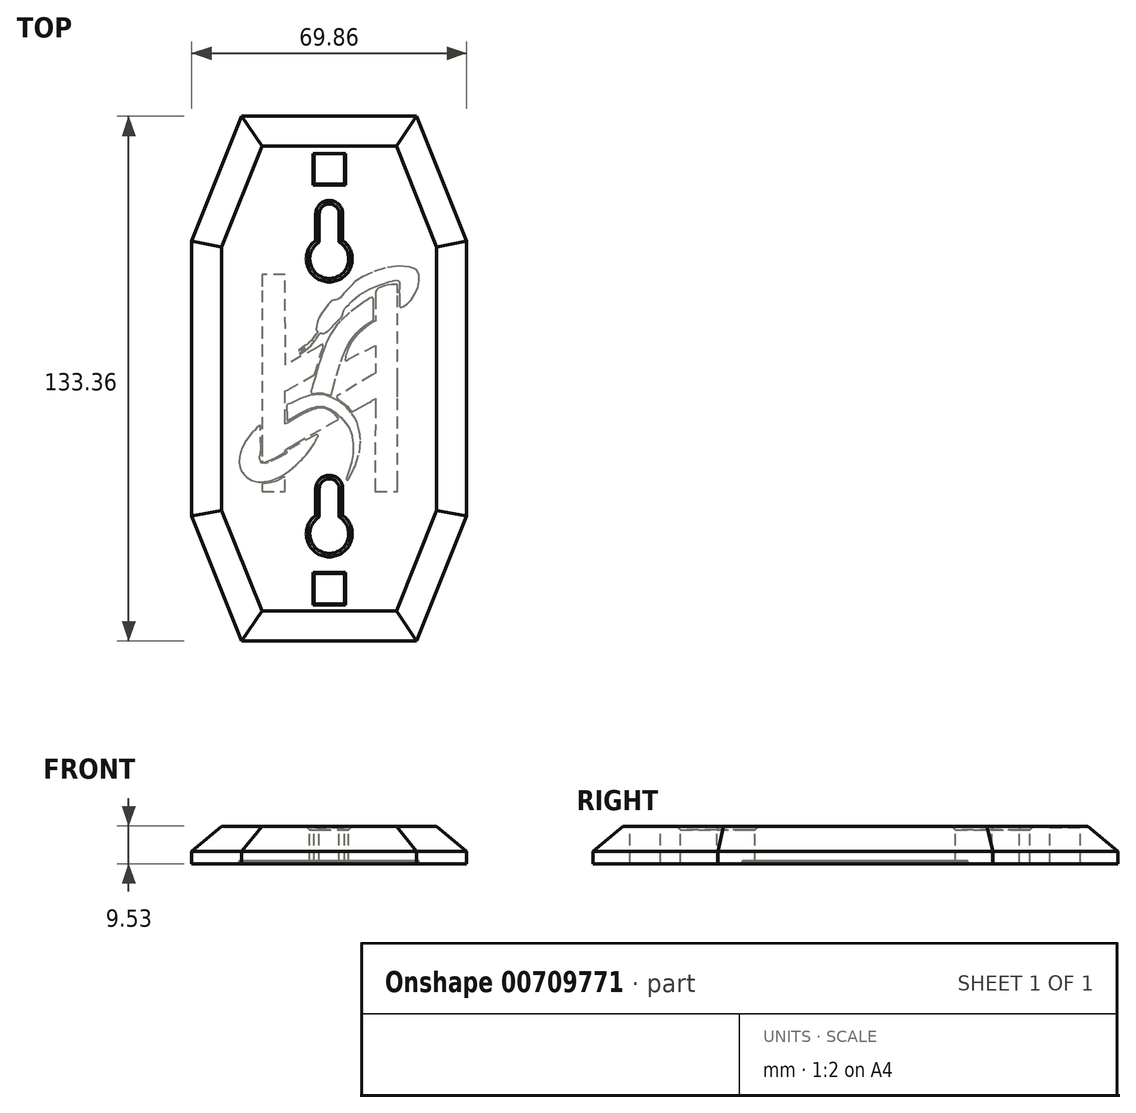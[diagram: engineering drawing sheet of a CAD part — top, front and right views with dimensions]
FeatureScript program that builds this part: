
annotation { "Feature Type Name" : "Feature", "Feature Type Description" : "" }
export const myFeature = defineFeature(function(context is Context, id is Id, definition is map)
    precondition{}
    {
        {
            var Q0;
            Q0=qCreatedBy(makeId("Top.planeOp"),FACE);
            var sketch = newSketch(context, id + "F0", { "sketchPlane" : qUnion([Q0])});
            skLineSegment(sketch, "E0.bottom", {"start": v(22.23, 66.68) * mm, "end": v(-22.22, 66.68) * mm});
            skLineSegment(sketch, "E0.top", {"start": v(22.22, -66.68) * mm, "end": v(-22.23, -66.68) * mm});
            skLineSegment(sketch, "E1.left", {"start": v(34.92, -34.93) * mm, "end": v(34.93, 34.92) * mm});
            skLineSegment(sketch, "E1.right", {"start": v(-34.93, -34.92) * mm, "end": v(-34.92, 34.93) * mm});
            skLineSegment(sketch, "E2", {"start": v(22.23, 66.67) * mm, "end": v(34.93, 34.92) * mm});
            skLineSegment(sketch, "E3", {"start": v(-22.22, 66.67) * mm, "end": v(-34.92, 34.93) * mm});
            skLineSegment(sketch, "E4", {"start": v(-34.93, -34.92) * mm, "end": v(-22.23, -66.68) * mm});
            skLineSegment(sketch, "E5", {"start": v(22.22, -66.68) * mm, "end": v(34.92, -34.93) * mm});
            skLineSegment(sketch, "E6", {"start": v(-17.37, -2.42) * mm, "end": v(-17.37, -0.22) * mm});
            skLineSegment(sketch, "E7", {"start": v(-17.37, -0.22) * mm, "end": v(-17.35, 21.74) * mm});
            skLineSegment(sketch, "E8", {"start": v(-17.35, 21.74) * mm, "end": v(-17.33, 23.94) * mm});
            skLineSegment(sketch, "E9", {"start": v(-17.33, 23.94) * mm, "end": v(-16.97, 23.94) * mm});
            skLineSegment(sketch, "E10", {"start": v(-16.97, 23.94) * mm, "end": v(-15.85, 23.92) * mm});
            skLineSegment(sketch, "E11", {"start": v(-15.85, 23.92) * mm, "end": v(-14.84, 23.83) * mm});
            skLineSegment(sketch, "E12", {"start": v(-14.84, 23.83) * mm, "end": v(-13.88, 23.56) * mm});
            skLineSegment(sketch, "E13", {"start": v(-13.88, 23.56) * mm, "end": v(-12.87, 23.15) * mm});
            skLineSegment(sketch, "E14", {"start": v(-12.87, 23.15) * mm, "end": v(-12.53, 23) * mm});
            skLineSegment(sketch, "E15", {"start": v(-12.53, 23) * mm, "end": v(-12.38, 22.93) * mm});
            skLineSegment(sketch, "E16", {"start": v(-12.38, 22.93) * mm, "end": v(-12, 22.53) * mm});
            skLineSegment(sketch, "E17", {"start": v(-12, 22.53) * mm, "end": v(-11.76, 21.9) * mm});
            skLineSegment(sketch, "E18", {"start": v(-11.76, 21.9) * mm, "end": v(-11.7, 21.25) * mm});
            skLineSegment(sketch, "E19", {"start": v(-11.7, 21.25) * mm, "end": v(-11.7, 20.85) * mm});
            skLineSegment(sketch, "E20", {"start": v(-11.7, 20.85) * mm, "end": v(-11.7, 20.71) * mm});
            skLineSegment(sketch, "E21", {"start": v(-11.7, 20.71) * mm, "end": v(-11.7, 14.62) * mm});
            skLineSegment(sketch, "E22", {"start": v(-11.7, 14.62) * mm, "end": v(-11.39, 14.51) * mm});
            skLineSegment(sketch, "E23", {"start": v(-11.39, 14.51) * mm, "end": v(-10.5, 14.04) * mm});
            skLineSegment(sketch, "E24", {"start": v(-10.5, 14.04) * mm, "end": v(-9.42, 13.27) * mm});
            skLineSegment(sketch, "E25", {"start": v(-9.42, 13.27) * mm, "end": v(-8.4, 12.4) * mm});
            skLineSegment(sketch, "E26", {"start": v(-8.4, 12.4) * mm, "end": v(-7.66, 11.74) * mm});
            skLineSegment(sketch, "E27", {"start": v(-7.66, 11.74) * mm, "end": v(-7.4, 11.53) * mm});
            skLineSegment(sketch, "E28", {"start": v(-7.4, 11.53) * mm, "end": v(-7.15, 11.32) * mm});
            skLineSegment(sketch, "E29", {"start": v(-7.15, 11.32) * mm, "end": v(-6.5, 10.61) * mm});
            skLineSegment(sketch, "E30", {"start": v(-6.5, 10.61) * mm, "end": v(-5.78, 9.57) * mm});
            skLineSegment(sketch, "E31", {"start": v(-5.78, 9.57) * mm, "end": v(-5.18, 8.44) * mm});
            skLineSegment(sketch, "E32", {"start": v(-5.18, 8.44) * mm, "end": v(-4.78, 7.57) * mm});
            skLineSegment(sketch, "E33", {"start": v(-4.78, 7.57) * mm, "end": v(-4.66, 7.28) * mm});
            skLineSegment(sketch, "E34", {"start": v(-4.66, 7.28) * mm, "end": v(-4.63, 7.18) * mm});
            skLineSegment(sketch, "E35", {"start": v(-4.63, 7.18) * mm, "end": v(-4.53, 6.89) * mm});
            skLineSegment(sketch, "E36", {"start": v(-4.53, 6.89) * mm, "end": v(-4.36, 6.39) * mm});
            skLineSegment(sketch, "E37", {"start": v(-4.36, 6.39) * mm, "end": v(-4.2, 5.84) * mm});
            skLineSegment(sketch, "E38", {"start": v(-4.2, 5.84) * mm, "end": v(-4.07, 5.33) * mm});
            skLineSegment(sketch, "E39", {"start": v(-4.07, 5.33) * mm, "end": v(-4.04, 4.91) * mm});
            skLineSegment(sketch, "E40", {"start": v(-4.04, 4.91) * mm, "end": v(-4.14, 4.66) * mm});
            skLineSegment(sketch, "E41", {"start": v(-4.14, 4.66) * mm, "end": v(-4.43, 4.66) * mm});
            skLineSegment(sketch, "E42", {"start": v(-4.43, 4.66) * mm, "end": v(-4.82, 4.88) * mm});
            skLineSegment(sketch, "E43", {"start": v(-4.82, 4.88) * mm, "end": v(-4.94, 4.97) * mm});
            skLineSegment(sketch, "E44", {"start": v(-4.94, 4.97) * mm, "end": v(-11.7, 8.43) * mm});
            skLineSegment(sketch, "E45", {"start": v(-11.7, 8.43) * mm, "end": v(-11.7, 1.45) * mm});
            skLineSegment(sketch, "E46", {"start": v(-11.7, 1.45) * mm, "end": v(-10.9, 1) * mm});
            skLineSegment(sketch, "E47", {"start": v(-10.9, 1) * mm, "end": v(-6.78, -1.51) * mm});
            skLineSegment(sketch, "E48", {"start": v(-6.78, -1.51) * mm, "end": v(-2.66, -4.02) * mm});
            skLineSegment(sketch, "E49", {"start": v(-2.66, -4.02) * mm, "end": v(-1.85, -4.48) * mm});
            skLineSegment(sketch, "E50", {"start": v(-1.85, -4.48) * mm, "end": v(-1.81, -4.54) * mm});
            skLineSegment(sketch, "E51", {"start": v(-1.81, -4.54) * mm, "end": v(-1.93, -4.9) * mm});
            skLineSegment(sketch, "E52", {"start": v(-1.93, -4.9) * mm, "end": v(-2.54, -5.38) * mm});
            skLineSegment(sketch, "E53", {"start": v(-2.54, -5.38) * mm, "end": v(-3.43, -6) * mm});
            skLineSegment(sketch, "E54", {"start": v(-3.43, -6) * mm, "end": v(-4.13, -6.56) * mm});
            skLineSegment(sketch, "E55", {"start": v(-4.13, -6.56) * mm, "end": v(-4.33, -6.78) * mm});
            skLineSegment(sketch, "E56", {"start": v(-4.33, -6.78) * mm, "end": v(-4.52, -6.96) * mm});
            skLineSegment(sketch, "E57", {"start": v(-4.52, -6.96) * mm, "end": v(-5.06, -7.56) * mm});
            skLineSegment(sketch, "E58", {"start": v(-5.06, -7.56) * mm, "end": v(-5.52, -8.12) * mm});
            skLineSegment(sketch, "E59", {"start": v(-5.52, -8.12) * mm, "end": v(-5.87, -8.36) * mm});
            skLineSegment(sketch, "E60", {"start": v(-5.87, -8.36) * mm, "end": v(-6.17, -8.24) * mm});
            skLineSegment(sketch, "E61", {"start": v(-6.17, -8.24) * mm, "end": v(-6.23, -8.17) * mm});
            skLineSegment(sketch, "E62", {"start": v(-6.23, -8.17) * mm, "end": v(-6.63, -7.95) * mm});
            skLineSegment(sketch, "E63", {"start": v(-6.63, -7.95) * mm, "end": v(-7.83, -7.3) * mm});
            skLineSegment(sketch, "E64", {"start": v(-7.83, -7.3) * mm, "end": v(-8.99, -6.65) * mm});
            skLineSegment(sketch, "E65", {"start": v(-8.99, -6.65) * mm, "end": v(-9.8, -6.19) * mm});
            skLineSegment(sketch, "E66", {"start": v(-9.8, -6.19) * mm, "end": v(-10.36, -5.87) * mm});
            skLineSegment(sketch, "E67", {"start": v(-10.36, -5.87) * mm, "end": v(-10.74, -5.64) * mm});
            skLineSegment(sketch, "E68", {"start": v(-10.74, -5.64) * mm, "end": v(-11.03, -5.46) * mm});
            skLineSegment(sketch, "E69", {"start": v(-11.03, -5.46) * mm, "end": v(-11.32, -5.28) * mm});
            skLineSegment(sketch, "E70", {"start": v(-11.32, -5.28) * mm, "end": v(-11.6, -5.11) * mm});
            skLineSegment(sketch, "E71", {"start": v(-11.6, -5.11) * mm, "end": v(-11.7, -5.06) * mm});
            skLineSegment(sketch, "E72", {"start": v(-11.7, -5.06) * mm, "end": v(-11.7, -7.02) * mm});
            skLineSegment(sketch, "E73", {"start": v(-11.7, -7.02) * mm, "end": v(-11.68, -26.64) * mm});
            skLineSegment(sketch, "E74", {"start": v(-11.68, -26.64) * mm, "end": v(-11.68, -28.6) * mm});
            skLineSegment(sketch, "E75", {"start": v(-11.68, -28.6) * mm, "end": v(-17.38, -28.6) * mm});
            skLineSegment(sketch, "E76", {"start": v(-17.38, -28.6) * mm, "end": v(-17.38, -26.42) * mm});
            skLineSegment(sketch, "E77", {"start": v(-17.38, -26.42) * mm, "end": v(-17.37, -4.6) * mm});
            skLineSegment(sketch, "E78", {"start": v(-17.37, -4.6) * mm, "end": v(-17.37, -2.42) * mm});
            skLineSegment(sketch, "E79", {"start": v(11.23, -25.1) * mm, "end": v(11.28, -25.05) * mm});
            skLineSegment(sketch, "E80", {"start": v(11.28, -25.05) * mm, "end": v(11.49, -25) * mm});
            skLineSegment(sketch, "E81", {"start": v(11.49, -25) * mm, "end": v(11.7, -25.09) * mm});
            skLineSegment(sketch, "E82", {"start": v(11.7, -25.09) * mm, "end": v(11.74, -25.12) * mm});
            skLineSegment(sketch, "E83", {"start": v(11.74, -25.12) * mm, "end": v(11.95, -25.23) * mm});
            skLineSegment(sketch, "E84", {"start": v(11.95, -25.23) * mm, "end": v(12.56, -25.55) * mm});
            skLineSegment(sketch, "E85", {"start": v(12.56, -25.55) * mm, "end": v(13.19, -25.86) * mm});
            skLineSegment(sketch, "E86", {"start": v(13.19, -25.86) * mm, "end": v(13.7, -26.09) * mm});
            skLineSegment(sketch, "E87", {"start": v(13.7, -26.09) * mm, "end": v(14.15, -26.25) * mm});
            skLineSegment(sketch, "E88", {"start": v(14.15, -26.25) * mm, "end": v(14.63, -26.37) * mm});
            skLineSegment(sketch, "E89", {"start": v(14.63, -26.37) * mm, "end": v(15.23, -26.5) * mm});
            skLineSegment(sketch, "E90", {"start": v(15.23, -26.5) * mm, "end": v(16, -26.63) * mm});
            skLineSegment(sketch, "E91", {"start": v(16, -26.63) * mm, "end": v(16.78, -26.77) * mm});
            skLineSegment(sketch, "E92", {"start": v(16.78, -26.77) * mm, "end": v(17.04, -26.81) * mm});
            skLineSegment(sketch, "E93", {"start": v(17.04, -26.81) * mm, "end": v(17.05, -27) * mm});
            skLineSegment(sketch, "E94", {"start": v(17.05, -27) * mm, "end": v(17.06, -27.6) * mm});
            skLineSegment(sketch, "E95", {"start": v(17.06, -27.6) * mm, "end": v(17.06, -27.7) * mm});
            skLineSegment(sketch, "E96", {"start": v(17.06, -27.7) * mm, "end": v(17.06, -27.82) * mm});
            skLineSegment(sketch, "E97", {"start": v(17.06, -27.82) * mm, "end": v(17.07, -28.4) * mm});
            skLineSegment(sketch, "E98", {"start": v(17.07, -28.4) * mm, "end": v(17.07, -28.6) * mm});
            skLineSegment(sketch, "E99", {"start": v(17.07, -28.6) * mm, "end": v(11.2, -28.6) * mm});
            skLineSegment(sketch, "E100", {"start": v(11.2, -28.6) * mm, "end": v(11.23, -25.1) * mm});
            skLineSegment(sketch, "E101", {"start": v(14.35, -25.69) * mm, "end": v(13.77, -25.5) * mm});
            skLineSegment(sketch, "E102", {"start": v(13.77, -25.5) * mm, "end": v(12.11, -24.69) * mm});
            skLineSegment(sketch, "E103", {"start": v(12.11, -24.69) * mm, "end": v(10.16, -23.4) * mm});
            skLineSegment(sketch, "E104", {"start": v(10.16, -23.4) * mm, "end": v(8.43, -21.96) * mm});
            skLineSegment(sketch, "E105", {"start": v(8.43, -21.96) * mm, "end": v(7.25, -20.84) * mm});
            skLineSegment(sketch, "E106", {"start": v(7.25, -20.84) * mm, "end": v(6.87, -20.46) * mm});
            skLineSegment(sketch, "E107", {"start": v(6.87, -20.46) * mm, "end": v(6.6, -20.15) * mm});
            skLineSegment(sketch, "E108", {"start": v(6.6, -20.15) * mm, "end": v(5.8, -19.2) * mm});
            skLineSegment(sketch, "E109", {"start": v(5.8, -19.2) * mm, "end": v(4.74, -17.91) * mm});
            skLineSegment(sketch, "E110", {"start": v(4.74, -17.91) * mm, "end": v(3.82, -16.57) * mm});
            skLineSegment(sketch, "E111", {"start": v(3.82, -16.57) * mm, "end": v(3.3, -15.55) * mm});
            skLineSegment(sketch, "E112", {"start": v(3.3, -15.55) * mm, "end": v(3.17, -15.18) * mm});
            skLineSegment(sketch, "E113", {"start": v(3.17, -15.18) * mm, "end": v(3.12, -15.08) * mm});
            skLineSegment(sketch, "E114", {"start": v(3.12, -15.08) * mm, "end": v(3.03, -14.76) * mm});
            skLineSegment(sketch, "E115", {"start": v(3, -14.34) * mm, "end": v(3.13, -14.12) * mm});
            skLineSegment(sketch, "E116", {"start": v(3.13, -14.12) * mm, "end": v(3.43, -14.24) * mm});
            skLineSegment(sketch, "E117", {"start": v(3.43, -14.24) * mm, "end": v(3.5, -14.31) * mm});
            skLineSegment(sketch, "E118", {"start": v(3.5, -14.31) * mm, "end": v(10.87, -18.35) * mm});
            skLineSegment(sketch, "E119", {"start": v(10.87, -18.35) * mm, "end": v(10.82, -18.45) * mm});
            skLineSegment(sketch, "E120", {"start": v(10.82, -18.45) * mm, "end": v(10.82, -18.81) * mm});
            skLineSegment(sketch, "E121", {"start": v(10.82, -18.81) * mm, "end": v(11.1, -19.12) * mm});
            skLineSegment(sketch, "E122", {"start": v(11.1, -19.12) * mm, "end": v(11.62, -19.38) * mm});
            skLineSegment(sketch, "E123", {"start": v(11.62, -19.38) * mm, "end": v(12.12, -19.62) * mm});
            skLineSegment(sketch, "E124", {"start": v(12.12, -19.62) * mm, "end": v(12.28, -19.71) * mm});
            skLineSegment(sketch, "E125", {"start": v(12.28, -19.71) * mm, "end": v(15.4, -21.26) * mm});
            skLineSegment(sketch, "E126", {"start": v(15.4, -21.26) * mm, "end": v(15.54, -21.35) * mm});
            skLineSegment(sketch, "E127", {"start": v(15.54, -21.35) * mm, "end": v(16.36, -21.6) * mm});
            skLineSegment(sketch, "E128", {"start": v(16.36, -21.6) * mm, "end": v(17.14, -21.4) * mm});
            skLineSegment(sketch, "E129", {"start": v(17.14, -21.4) * mm, "end": v(17.27, -21.27) * mm});
            skLineSegment(sketch, "E130", {"start": v(17.27, -21.27) * mm, "end": v(17.33, -21.15) * mm});
            skLineSegment(sketch, "E131", {"start": v(17.33, -21.15) * mm, "end": v(17.5, -20.8) * mm});
            skLineSegment(sketch, "E132", {"start": v(17.5, -20.8) * mm, "end": v(17.7, -20.32) * mm});
            skLineSegment(sketch, "E133", {"start": v(17.7, -20.32) * mm, "end": v(17.76, -19.83) * mm});
            skLineSegment(sketch, "E134", {"start": v(17.76, -19.83) * mm, "end": v(17.62, -19.46) * mm});
            skLineSegment(sketch, "E135", {"start": v(17.62, -19.46) * mm, "end": v(17.53, -19.37) * mm});
            skLineSegment(sketch, "E136", {"start": v(17.53, -19.37) * mm, "end": v(17.51, -19.36) * mm});
            skLineSegment(sketch, "E137", {"start": v(17.51, -19.36) * mm, "end": v(17.43, -19.37) * mm});
            skLineSegment(sketch, "E138", {"start": v(17.43, -19.37) * mm, "end": v(17.4, -19.36) * mm});
            skLineSegment(sketch, "E139", {"start": v(17.4, -19.36) * mm, "end": v(17.41, -19.07) * mm});
            skLineSegment(sketch, "E140", {"start": v(17.41, -19.07) * mm, "end": v(17.4, -18.48) * mm});
            skLineSegment(sketch, "E141", {"start": v(17.4, -18.48) * mm, "end": v(17.4, -18.28) * mm});
            skLineSegment(sketch, "E142", {"start": v(17.4, -18.28) * mm, "end": v(17.4, -17.77) * mm});
            skLineSegment(sketch, "E143", {"start": v(17.4, -17.77) * mm, "end": v(17.4, -12.63) * mm});
            skLineSegment(sketch, "E144", {"start": v(17.4, -12.63) * mm, "end": v(17.41, -12.11) * mm});
            skLineSegment(sketch, "E145", {"start": v(17.41, -12.11) * mm, "end": v(17.41, -12.03) * mm});
            skLineSegment(sketch, "E146", {"start": v(17.41, -12.03) * mm, "end": v(17.54, -11.79) * mm});
            skLineSegment(sketch, "E147", {"start": v(17.54, -11.79) * mm, "end": v(17.9, -12) * mm});
            skLineSegment(sketch, "E148", {"start": v(17.9, -12) * mm, "end": v(18.45, -12.57) * mm});
            skLineSegment(sketch, "E149", {"start": v(18.45, -12.57) * mm, "end": v(18.98, -13.12) * mm});
            skLineSegment(sketch, "E150", {"start": v(18.98, -13.12) * mm, "end": v(19.17, -13.3) * mm});
            skLineSegment(sketch, "E151", {"start": v(19.17, -13.3) * mm, "end": v(19.56, -13.68) * mm});
            skLineSegment(sketch, "E152", {"start": v(19.56, -13.68) * mm, "end": v(21.14, -15.67) * mm});
            skLineSegment(sketch, "E153", {"start": v(21.14, -15.67) * mm, "end": v(22.28, -17.86) * mm});
            skLineSegment(sketch, "E154", {"start": v(22.28, -17.86) * mm, "end": v(22.46, -18.34) * mm});
            skLineSegment(sketch, "E155", {"start": v(22.46, -18.34) * mm, "end": v(22.54, -18.7) * mm});
            skLineSegment(sketch, "E156", {"start": v(22.54, -18.7) * mm, "end": v(22.75, -19.83) * mm});
            skLineSegment(sketch, "E157", {"start": v(22.75, -19.83) * mm, "end": v(22.86, -21.25) * mm});
            skLineSegment(sketch, "E158", {"start": v(22.86, -21.25) * mm, "end": v(22.65, -22.6) * mm});
            skLineSegment(sketch, "E159", {"start": v(22.65, -22.6) * mm, "end": v(22.21, -23.59) * mm});
            skLineSegment(sketch, "E160", {"start": v(22.21, -23.59) * mm, "end": v(22, -23.87) * mm});
            skLineSegment(sketch, "E161", {"start": v(22, -23.87) * mm, "end": v(21.77, -24.22) * mm});
            skLineSegment(sketch, "E162", {"start": v(21.77, -24.22) * mm, "end": v(20.89, -25.15) * mm});
            skLineSegment(sketch, "E163", {"start": v(20.89, -25.15) * mm, "end": v(19.6, -25.92) * mm});
            skLineSegment(sketch, "E164", {"start": v(19.6, -25.92) * mm, "end": v(18.15, -26.25) * mm});
            skLineSegment(sketch, "E165", {"start": v(18.15, -26.25) * mm, "end": v(16.95, -26.25) * mm});
            skLineSegment(sketch, "E166", {"start": v(16.95, -26.25) * mm, "end": v(16.56, -26.2) * mm});
            skLineSegment(sketch, "E167", {"start": v(16.56, -26.2) * mm, "end": v(16.45, -26.18) * mm});
            skLineSegment(sketch, "E168", {"start": v(16.45, -26.18) * mm, "end": v(16.1, -26.11) * mm});
            skLineSegment(sketch, "E169", {"start": v(16.1, -26.11) * mm, "end": v(15.46, -26) * mm});
            skLineSegment(sketch, "E170", {"start": v(15.46, -26) * mm, "end": v(14.82, -25.84) * mm});
            skLineSegment(sketch, "E171", {"start": v(14.82, -25.84) * mm, "end": v(14.46, -25.74) * mm});
            skLineSegment(sketch, "E172", {"start": v(14.46, -25.74) * mm, "end": v(14.35, -25.69) * mm});
            skLineSegment(sketch, "E173", {"start": v(-4.77, -25.69) * mm, "end": v(-4.9, -25.47) * mm});
            skLineSegment(sketch, "E174", {"start": v(-4.9, -25.47) * mm, "end": v(-5.48, -24.31) * mm});
            skLineSegment(sketch, "E175", {"start": v(-5.48, -24.31) * mm, "end": v(-6.06, -23.16) * mm});
            skLineSegment(sketch, "E176", {"start": v(-6.06, -23.16) * mm, "end": v(-6.2, -22.94) * mm});
            skLineSegment(sketch, "E177", {"start": v(-6.2, -22.94) * mm, "end": v(-6.51, -22.26) * mm});
            skLineSegment(sketch, "E178", {"start": v(-6.51, -22.26) * mm, "end": v(-7.66, -18.85) * mm});
            skLineSegment(sketch, "E179", {"start": v(-7.66, -18.85) * mm, "end": v(-7.97, -15.4) * mm});
            skLineSegment(sketch, "E180", {"start": v(-7.97, -15.4) * mm, "end": v(-7.86, -14.7) * mm});
            skLineSegment(sketch, "E181", {"start": v(-7.86, -14.7) * mm, "end": v(-7.8, -14.17) * mm});
            skLineSegment(sketch, "E182", {"start": v(-7.8, -14.17) * mm, "end": v(-7.5, -12.57) * mm});
            skLineSegment(sketch, "E183", {"start": v(-7.5, -12.57) * mm, "end": v(-7.01, -11.03) * mm});
            skLineSegment(sketch, "E184", {"start": v(-7.01, -11.03) * mm, "end": v(-6.4, -9.82) * mm});
            skLineSegment(sketch, "E185", {"start": v(-6.4, -9.82) * mm, "end": v(-5.83, -8.98) * mm});
            skLineSegment(sketch, "E186", {"start": v(-5.83, -8.98) * mm, "end": v(-5.63, -8.71) * mm});
            skLineSegment(sketch, "E187", {"start": v(-5.63, -8.71) * mm, "end": v(-5.43, -8.42) * mm});
            skLineSegment(sketch, "E188", {"start": v(-5.43, -8.42) * mm, "end": v(-4.23, -7.13) * mm});
            skLineSegment(sketch, "E189", {"start": v(-4.23, -7.13) * mm, "end": v(-2.85, -6.01) * mm});
            skLineSegment(sketch, "E190", {"start": v(-2.85, -6.01) * mm, "end": v(-2.56, -5.81) * mm});
            skLineSegment(sketch, "E191", {"start": v(-2.56, -5.81) * mm, "end": v(-2.08, -5.54) * mm});
            skLineSegment(sketch, "E192", {"start": v(-2.08, -5.54) * mm, "end": v(-0.59, -4.78) * mm});
            skLineSegment(sketch, "E193", {"start": v(-0.59, -4.78) * mm, "end": v(1.02, -4.18) * mm});
            skLineSegment(sketch, "E194", {"start": v(1.02, -4.18) * mm, "end": v(2.49, -3.96) * mm});
            skLineSegment(sketch, "E195", {"start": v(2.49, -3.96) * mm, "end": v(3.66, -4.03) * mm});
            skLineSegment(sketch, "E196", {"start": v(3.66, -4.03) * mm, "end": v(4.04, -4.1) * mm});
            skLineSegment(sketch, "E197", {"start": v(4.04, -4.1) * mm, "end": v(4.6, -4.18) * mm});
            skLineSegment(sketch, "E198", {"start": v(4.6, -4.18) * mm, "end": v(7.3, -5.07) * mm});
            skLineSegment(sketch, "E199", {"start": v(7.3, -5.07) * mm, "end": v(9.85, -6.25) * mm});
            skLineSegment(sketch, "E200", {"start": v(9.85, -6.25) * mm, "end": v(10.31, -6.48) * mm});
            skLineSegment(sketch, "E201", {"start": v(10.31, -6.48) * mm, "end": v(10.4, -6.5) * mm});
            skLineSegment(sketch, "E202", {"start": v(10.4, -6.5) * mm, "end": v(10.66, -6.65) * mm});
            skLineSegment(sketch, "E203", {"start": v(10.66, -6.65) * mm, "end": v(10.8, -6.94) * mm});
            skLineSegment(sketch, "E204", {"start": v(10.8, -6.94) * mm, "end": v(10.81, -7.32) * mm});
            skLineSegment(sketch, "E205", {"start": v(10.81, -7.32) * mm, "end": v(10.8, -7.61) * mm});
            skLineSegment(sketch, "E206", {"start": v(10.8, -7.61) * mm, "end": v(10.8, -7.7) * mm});
            skLineSegment(sketch, "E207", {"start": v(10.8, -7.7) * mm, "end": v(10.8, -7.92) * mm});
            skLineSegment(sketch, "E208", {"start": v(10.8, -7.92) * mm, "end": v(10.78, -8.54) * mm});
            skLineSegment(sketch, "E209", {"start": v(10.78, -8.54) * mm, "end": v(10.76, -8.97) * mm});
            skLineSegment(sketch, "E210", {"start": v(10.76, -8.97) * mm, "end": v(10.75, -9.13) * mm});
            skLineSegment(sketch, "E211", {"start": v(10.75, -9.13) * mm, "end": v(10.75, -9.15) * mm});
            skLineSegment(sketch, "E212", {"start": v(10.75, -9.15) * mm, "end": v(10.75, -9.17) * mm});
            skLineSegment(sketch, "E213", {"start": v(10.75, -9.17) * mm, "end": v(10.75, -9.33) * mm});
            skLineSegment(sketch, "E214", {"start": v(10.75, -9.33) * mm, "end": v(10.73, -9.76) * mm});
            skLineSegment(sketch, "E215", {"start": v(10.73, -9.76) * mm, "end": v(10.7, -10.38) * mm});
            skLineSegment(sketch, "E216", {"start": v(10.7, -10.38) * mm, "end": v(10.7, -10.59) * mm});
            skLineSegment(sketch, "E217", {"start": v(10.7, -10.59) * mm, "end": v(10.24, -10.35) * mm});
            skLineSegment(sketch, "E218", {"start": v(10.24, -10.35) * mm, "end": v(8.86, -9.64) * mm});
            skLineSegment(sketch, "E219", {"start": v(8.86, -9.64) * mm, "end": v(7.5, -8.9) * mm});
            skLineSegment(sketch, "E220", {"start": v(7.5, -8.9) * mm, "end": v(6.52, -8.35) * mm});
            skLineSegment(sketch, "E221", {"start": v(6.52, -8.35) * mm, "end": v(5.8, -7.95) * mm});
            skLineSegment(sketch, "E222", {"start": v(5.8, -7.95) * mm, "end": v(5.21, -7.66) * mm});
            skLineSegment(sketch, "E223", {"start": v(5.21, -7.66) * mm, "end": v(4.68, -7.45) * mm});
            skLineSegment(sketch, "E224", {"start": v(4.68, -7.45) * mm, "end": v(4.07, -7.28) * mm});
            skLineSegment(sketch, "E225", {"start": v(4.07, -7.28) * mm, "end": v(3.48, -7.15) * mm});
            skLineSegment(sketch, "E226", {"start": v(3.48, -7.15) * mm, "end": v(3.28, -7.12) * mm});
            skLineSegment(sketch, "E227", {"start": v(3.28, -7.12) * mm, "end": v(2.83, -7.04) * mm});
            skLineSegment(sketch, "E228", {"start": v(2.83, -7.04) * mm, "end": v(1.42, -7.13) * mm});
            skLineSegment(sketch, "E229", {"start": v(1.42, -7.13) * mm, "end": v(-0.16, -7.7) * mm});
            skLineSegment(sketch, "E230", {"start": v(-0.16, -7.7) * mm, "end": v(-1.54, -8.63) * mm});
            skLineSegment(sketch, "E231", {"start": v(-1.54, -8.63) * mm, "end": v(-2.5, -9.42) * mm});
            skLineSegment(sketch, "E232", {"start": v(-2.5, -9.42) * mm, "end": v(-2.82, -9.68) * mm});
            skLineSegment(sketch, "E233", {"start": v(-2.82, -9.68) * mm, "end": v(-2.99, -9.88) * mm});
            skLineSegment(sketch, "E234", {"start": v(-2.99, -9.88) * mm, "end": v(-3.52, -10.44) * mm});
            skLineSegment(sketch, "E235", {"start": v(-3.52, -10.44) * mm, "end": v(-4.33, -11.39) * mm});
            skLineSegment(sketch, "E236", {"start": v(-4.33, -11.39) * mm, "end": v(-5.1, -12.68) * mm});
            skLineSegment(sketch, "E237", {"start": v(-5.1, -12.68) * mm, "end": v(-5.61, -14) * mm});
            skLineSegment(sketch, "E238", {"start": v(-5.61, -14) * mm, "end": v(-5.72, -14.46) * mm});
            skLineSegment(sketch, "E239", {"start": v(-5.72, -14.46) * mm, "end": v(-5.79, -14.93) * mm});
            skLineSegment(sketch, "E240", {"start": v(-5.79, -14.93) * mm, "end": v(-5.98, -16.34) * mm});
            skLineSegment(sketch, "E241", {"start": v(-5.98, -16.34) * mm, "end": v(-6.08, -17.65) * mm});
            skLineSegment(sketch, "E242", {"start": v(-6.08, -17.65) * mm, "end": v(-6, -19) * mm});
            skLineSegment(sketch, "E243", {"start": v(-6, -19) * mm, "end": v(-5.8, -20.54) * mm});
            skLineSegment(sketch, "E244", {"start": v(-5.8, -20.54) * mm, "end": v(-5.72, -21.05) * mm});
            skLineSegment(sketch, "E245", {"start": v(-5.72, -21.05) * mm, "end": v(-5.64, -21.31) * mm});
            skLineSegment(sketch, "E246", {"start": v(-5.64, -21.31) * mm, "end": v(-5.41, -22.09) * mm});
            skLineSegment(sketch, "E247", {"start": v(-5.41, -22.09) * mm, "end": v(-5.05, -23.3) * mm});
            skLineSegment(sketch, "E248", {"start": v(-5.05, -23.3) * mm, "end": v(-4.67, -24.51) * mm});
            skLineSegment(sketch, "E249", {"start": v(-4.67, -24.51) * mm, "end": v(-4.42, -25.28) * mm});
            skLineSegment(sketch, "E250", {"start": v(-4.42, -25.28) * mm, "end": v(-4.32, -25.54) * mm});
            skLineSegment(sketch, "E251", {"start": v(-4.32, -25.54) * mm, "end": v(-4.34, -25.58) * mm});
            skLineSegment(sketch, "E252", {"start": v(-4.34, -25.58) * mm, "end": v(-4.51, -25.75) * mm});
            skLineSegment(sketch, "E253", {"start": v(-4.51, -25.75) * mm, "end": v(-4.75, -25.73) * mm});
            skLineSegment(sketch, "E254", {"start": v(-4.75, -25.73) * mm, "end": v(-4.77, -25.69) * mm});
            skLineSegment(sketch, "E255", {"start": v(16.59, -21.33) * mm, "end": v(16.13, -21.18) * mm});
            skLineSegment(sketch, "E256", {"start": v(16.13, -21.18) * mm, "end": v(13.82, -20.2) * mm});
            skLineSegment(sketch, "E257", {"start": v(13.82, -20.2) * mm, "end": v(11.6, -18.91) * mm});
            skLineSegment(sketch, "E258", {"start": v(11.6, -18.91) * mm, "end": v(11.19, -18.6) * mm});
            skLineSegment(sketch, "E259", {"start": v(11.19, -18.6) * mm, "end": v(11.23, -18.53) * mm});
            skLineSegment(sketch, "E260", {"start": v(11.23, -18.53) * mm, "end": v(11.19, -18.2) * mm});
            skLineSegment(sketch, "E261", {"start": v(11.19, -18.2) * mm, "end": v(10.82, -17.85) * mm});
            skLineSegment(sketch, "E262", {"start": v(10.82, -17.85) * mm, "end": v(10.27, -17.52) * mm});
            skLineSegment(sketch, "E263", {"start": v(10.27, -17.52) * mm, "end": v(9.86, -17.28) * mm});
            skLineSegment(sketch, "E264", {"start": v(9.86, -17.28) * mm, "end": v(9.74, -17.19) * mm});
            skLineSegment(sketch, "E265", {"start": v(9.74, -17.19) * mm, "end": v(8.73, -16.61) * mm});
            skLineSegment(sketch, "E266", {"start": v(8.73, -16.61) * mm, "end": v(-1.33, -10.9) * mm});
            skLineSegment(sketch, "E267", {"start": v(-1.33, -10.9) * mm, "end": v(-2.33, -10.31) * mm});
            skLineSegment(sketch, "E268", {"start": v(-2.33, -10.31) * mm, "end": v(-2.23, -10.01) * mm});
            skLineSegment(sketch, "E269", {"start": v(-2.23, -10.01) * mm, "end": v(-1.65, -9.2) * mm});
            skLineSegment(sketch, "E270", {"start": v(-1.65, -9.2) * mm, "end": v(-0.57, -8.33) * mm});
            skLineSegment(sketch, "E271", {"start": v(-0.57, -8.33) * mm, "end": v(0.72, -7.72) * mm});
            skLineSegment(sketch, "E272", {"start": v(0.72, -7.72) * mm, "end": v(1.7, -7.46) * mm});
            skLineSegment(sketch, "E273", {"start": v(1.7, -7.46) * mm, "end": v(2.04, -7.42) * mm});
            skLineSegment(sketch, "E274", {"start": v(2.04, -7.42) * mm, "end": v(2.66, -7.46) * mm});
            skLineSegment(sketch, "E275", {"start": v(2.66, -7.46) * mm, "end": v(4.5, -7.95) * mm});
            skLineSegment(sketch, "E276", {"start": v(4.5, -7.95) * mm, "end": v(6.79, -8.99) * mm});
            skLineSegment(sketch, "E277", {"start": v(6.79, -8.99) * mm, "end": v(8.98, -10.26) * mm});
            skLineSegment(sketch, "E278", {"start": v(8.98, -10.26) * mm, "end": v(10.62, -11.2) * mm});
            skLineSegment(sketch, "E279", {"start": v(10.62, -11.2) * mm, "end": v(11.19, -11.49) * mm});
            skLineSegment(sketch, "E280", {"start": v(11.19, -11.49) * mm, "end": v(11.2, -10.8) * mm});
            skLineSegment(sketch, "E281", {"start": v(11.2, -10.8) * mm, "end": v(11.2, -3.87) * mm});
            skLineSegment(sketch, "E282", {"start": v(11.2, -3.87) * mm, "end": v(11.2, -3.17) * mm});
            skLineSegment(sketch, "E283", {"start": v(11.2, -3.17) * mm, "end": v(10.58, -2.83) * mm});
            skLineSegment(sketch, "E284", {"start": v(10.58, -2.83) * mm, "end": v(4.4, 0.66) * mm});
            skLineSegment(sketch, "E285", {"start": v(4.4, 0.66) * mm, "end": v(3.78, 1.01) * mm});
            skLineSegment(sketch, "E286", {"start": v(3.78, 1.01) * mm, "end": v(2.07, 6.67) * mm});
            skLineSegment(sketch, "E287", {"start": v(2.07, 6.67) * mm, "end": v(2, 6.88) * mm});
            skLineSegment(sketch, "E288", {"start": v(2, 6.88) * mm, "end": v(1.77, 7.51) * mm});
            skLineSegment(sketch, "E289", {"start": v(1.77, 7.51) * mm, "end": v(1.6, 8.1) * mm});
            skLineSegment(sketch, "E290", {"start": v(1.6, 8.1) * mm, "end": v(1.54, 8.48) * mm});
            skLineSegment(sketch, "E291", {"start": v(1.54, 8.48) * mm, "end": v(1.6, 8.65) * mm});
            skLineSegment(sketch, "E292", {"start": v(1.6, 8.65) * mm, "end": v(1.79, 8.65) * mm});
            skLineSegment(sketch, "E293", {"start": v(1.79, 8.65) * mm, "end": v(2.1, 8.52) * mm});
            skLineSegment(sketch, "E294", {"start": v(2.1, 8.52) * mm, "end": v(2.52, 8.27) * mm});
            skLineSegment(sketch, "E295", {"start": v(2.52, 8.27) * mm, "end": v(2.93, 8.02) * mm});
            skLineSegment(sketch, "E296", {"start": v(2.93, 8.02) * mm, "end": v(3.07, 7.93) * mm});
            skLineSegment(sketch, "E297", {"start": v(3.07, 7.93) * mm, "end": v(11.13, 3.5) * mm});
            skLineSegment(sketch, "E298", {"start": v(11.13, 3.5) * mm, "end": v(11.2, 26.4) * mm});
            skLineSegment(sketch, "E299", {"start": v(11.2, 26.4) * mm, "end": v(17.03, 26.4) * mm});
            skLineSegment(sketch, "E300", {"start": v(17.03, 26.4) * mm, "end": v(17.04, 22.46) * mm});
            skLineSegment(sketch, "E301", {"start": v(17.04, 22.46) * mm, "end": v(17.06, -16.8) * mm});
            skLineSegment(sketch, "E302", {"start": v(17.06, -16.8) * mm, "end": v(17.04, -20.74) * mm});
            skLineSegment(sketch, "E303", {"start": v(17.04, -20.74) * mm, "end": v(17.03, -20.8) * mm});
            skLineSegment(sketch, "E304", {"start": v(17.03, -20.8) * mm, "end": v(16.9, -21.13) * mm});
            skLineSegment(sketch, "E305", {"start": v(16.9, -21.13) * mm, "end": v(16.65, -21.33) * mm});
            skLineSegment(sketch, "E306", {"start": v(16.65, -21.33) * mm, "end": v(16.59, -21.33) * mm});
            skLineSegment(sketch, "E307", {"start": v(-0.68, -3.5) * mm, "end": v(-0.82, -2.9) * mm});
            skLineSegment(sketch, "E308", {"start": v(-0.82, -2.9) * mm, "end": v(-1.8, 0.83) * mm});
            skLineSegment(sketch, "E309", {"start": v(-1.8, 0.83) * mm, "end": v(-2.93, 4.36) * mm});
            skLineSegment(sketch, "E310", {"start": v(-2.93, 4.36) * mm, "end": v(-3.23, 5.08) * mm});
            skLineSegment(sketch, "E311", {"start": v(-3.23, 5.08) * mm, "end": v(-3.4, 5.56) * mm});
            skLineSegment(sketch, "E312", {"start": v(-3.4, 5.56) * mm, "end": v(-3.97, 6.98) * mm});
            skLineSegment(sketch, "E313", {"start": v(-3.97, 6.98) * mm, "end": v(-4.68, 8.48) * mm});
            skLineSegment(sketch, "E314", {"start": v(-4.68, 8.48) * mm, "end": v(-5.5, 9.8) * mm});
            skLineSegment(sketch, "E315", {"start": v(-5.5, 9.8) * mm, "end": v(-6.25, 10.81) * mm});
            skLineSegment(sketch, "E316", {"start": v(-6.25, 10.81) * mm, "end": v(-6.51, 11.14) * mm});
            skLineSegment(sketch, "E317", {"start": v(-6.51, 11.14) * mm, "end": v(-6.78, 11.46) * mm});
            skLineSegment(sketch, "E318", {"start": v(-6.78, 11.46) * mm, "end": v(-7.66, 12.37) * mm});
            skLineSegment(sketch, "E319", {"start": v(-7.66, 12.37) * mm, "end": v(-8.8, 13.34) * mm});
            skLineSegment(sketch, "E320", {"start": v(-8.8, 13.34) * mm, "end": v(-9.95, 14.14) * mm});
            skLineSegment(sketch, "E321", {"start": v(-9.95, 14.14) * mm, "end": v(-10.88, 14.7) * mm});
            skLineSegment(sketch, "E322", {"start": v(-10.88, 14.7) * mm, "end": v(-11.2, 14.87) * mm});
            skLineSegment(sketch, "E323", {"start": v(-11.2, 14.87) * mm, "end": v(-11.2, 15.39) * mm});
            skLineSegment(sketch, "E324", {"start": v(-11.2, 15.39) * mm, "end": v(-11.2, 17.55) * mm});
            skLineSegment(sketch, "E325", {"start": v(-11.2, 17.55) * mm, "end": v(-11.2, 19.57) * mm});
            skLineSegment(sketch, "E326", {"start": v(-11.2, 19.57) * mm, "end": v(-11.2, 20.02) * mm});
            skLineSegment(sketch, "E327", {"start": v(-11.2, 20.02) * mm, "end": v(-11.2, 20.12) * mm});
            skLineSegment(sketch, "E328", {"start": v(-11.2, 20.12) * mm, "end": v(-11.16, 20.43) * mm});
            skLineSegment(sketch, "E329", {"start": v(-11.16, 20.43) * mm, "end": v(-11, 20.61) * mm});
            skLineSegment(sketch, "E330", {"start": v(-11, 20.61) * mm, "end": v(-10.72, 20.61) * mm});
            skLineSegment(sketch, "E331", {"start": v(-10.72, 20.61) * mm, "end": v(-10.36, 20.46) * mm});
            skLineSegment(sketch, "E332", {"start": v(-10.36, 20.46) * mm, "end": v(-9.93, 20.2) * mm});
            skLineSegment(sketch, "E333", {"start": v(-9.93, 20.2) * mm, "end": v(-9.47, 19.9) * mm});
            skLineSegment(sketch, "E334", {"start": v(-9.47, 19.9) * mm, "end": v(-8.99, 19.55) * mm});
            skLineSegment(sketch, "E335", {"start": v(-8.99, 19.55) * mm, "end": v(-8.63, 19.32) * mm});
            skLineSegment(sketch, "E336", {"start": v(-8.63, 19.32) * mm, "end": v(-8.51, 19.24) * mm});
            skLineSegment(sketch, "E337", {"start": v(-8.51, 19.24) * mm, "end": v(-7.96, 18.86) * mm});
            skLineSegment(sketch, "E338", {"start": v(-7.96, 18.86) * mm, "end": v(-5.2, 16.85) * mm});
            skLineSegment(sketch, "E339", {"start": v(-5.2, 16.85) * mm, "end": v(-2.77, 14.62) * mm});
            skLineSegment(sketch, "E340", {"start": v(-2.77, 14.62) * mm, "end": v(-2.38, 14.13) * mm});
            skLineSegment(sketch, "E341", {"start": v(-2.38, 14.13) * mm, "end": v(-1.98, 13.7) * mm});
            skLineSegment(sketch, "E342", {"start": v(-1.98, 13.7) * mm, "end": v(-0.41, 11.42) * mm});
            skLineSegment(sketch, "E343", {"start": v(-0.41, 11.42) * mm, "end": v(0.77, 9) * mm});
            skLineSegment(sketch, "E344", {"start": v(0.77, 9) * mm, "end": v(0.97, 8.5) * mm});
            skLineSegment(sketch, "E345", {"start": v(0.97, 8.5) * mm, "end": v(1.1, 8.16) * mm});
            skLineSegment(sketch, "E346", {"start": v(1.1, 8.16) * mm, "end": v(1.46, 7.13) * mm});
            skLineSegment(sketch, "E347", {"start": v(1.46, 7.13) * mm, "end": v(1.82, 6.1) * mm});
            skLineSegment(sketch, "E348", {"start": v(1.82, 6.1) * mm, "end": v(2.12, 5.27) * mm});
            skLineSegment(sketch, "E349", {"start": v(2.12, 5.27) * mm, "end": v(2.4, 4.44) * mm});
            skLineSegment(sketch, "E350", {"start": v(2.4, 4.44) * mm, "end": v(2.7, 3.43) * mm});
            skLineSegment(sketch, "E351", {"start": v(2.7, 3.43) * mm, "end": v(3.11, 2.08) * mm});
            skLineSegment(sketch, "E352", {"start": v(3.11, 2.08) * mm, "end": v(3.65, 0.2) * mm});
            skLineSegment(sketch, "E353", {"start": v(3.65, 0.2) * mm, "end": v(4.2, -1.72) * mm});
            skLineSegment(sketch, "E354", {"start": v(4.2, -1.72) * mm, "end": v(4.38, -2.36) * mm});
            skLineSegment(sketch, "E355", {"start": v(4.38, -2.36) * mm, "end": v(4.43, -2.5) * mm});
            skLineSegment(sketch, "E356", {"start": v(4.43, -2.5) * mm, "end": v(4.57, -2.97) * mm});
            skLineSegment(sketch, "E357", {"start": v(4.57, -2.97) * mm, "end": v(4.62, -3.36) * mm});
            skLineSegment(sketch, "E358", {"start": v(4.62, -3.36) * mm, "end": v(4.52, -3.6) * mm});
            skLineSegment(sketch, "E359", {"start": v(4.52, -3.6) * mm, "end": v(4.29, -3.7) * mm});
            skLineSegment(sketch, "E360", {"start": v(4.29, -3.7) * mm, "end": v(3.92, -3.72) * mm});
            skLineSegment(sketch, "E361", {"start": v(3.92, -3.72) * mm, "end": v(3.42, -3.7) * mm});
            skLineSegment(sketch, "E362", {"start": v(3.42, -3.7) * mm, "end": v(2.78, -3.65) * mm});
            skLineSegment(sketch, "E363", {"start": v(2.78, -3.65) * mm, "end": v(2.22, -3.64) * mm});
            skLineSegment(sketch, "E364", {"start": v(2.22, -3.64) * mm, "end": v(2.03, -3.65) * mm});
            skLineSegment(sketch, "E365", {"start": v(2.03, -3.65) * mm, "end": v(1.94, -3.65) * mm});
            skLineSegment(sketch, "E366", {"start": v(1.94, -3.65) * mm, "end": v(1.7, -3.7) * mm});
            skLineSegment(sketch, "E367", {"start": v(1.7, -3.7) * mm, "end": v(1.27, -3.8) * mm});
            skLineSegment(sketch, "E368", {"start": v(1.27, -3.8) * mm, "end": v(0.8, -3.92) * mm});
            skLineSegment(sketch, "E369", {"start": v(0.8, -3.92) * mm, "end": v(0.34, -4.03) * mm});
            skLineSegment(sketch, "E370", {"start": v(0.34, -4.03) * mm, "end": v(-0.08, -4.1) * mm});
            skLineSegment(sketch, "E371", {"start": v(-0.08, -4.1) * mm, "end": v(-0.4, -4.1) * mm});
            skLineSegment(sketch, "E372", {"start": v(-0.4, -4.1) * mm, "end": v(-0.58, -3.98) * mm});
            skLineSegment(sketch, "E373", {"start": v(-0.58, -3.98) * mm, "end": v(-0.6, -3.8) * mm});
            skLineSegment(sketch, "E374", {"start": v(-0.6, -3.8) * mm, "end": v(-0.68, -3.5) * mm});
            skLineSegment(sketch, "E375", {"start": v(3.48, 9.86) * mm, "end": v(3.33, 10.11) * mm});
            skLineSegment(sketch, "E376", {"start": v(3.33, 10.11) * mm, "end": v(2.85, 10.85) * mm});
            skLineSegment(sketch, "E377", {"start": v(2.85, 10.85) * mm, "end": v(2.43, 11.37) * mm});
            skLineSegment(sketch, "E378", {"start": v(2.43, 11.37) * mm, "end": v(2.15, 11.56) * mm});
            skLineSegment(sketch, "E379", {"start": v(2.15, 11.56) * mm, "end": v(1.94, 11.56) * mm});
            skLineSegment(sketch, "E380", {"start": v(1.94, 11.56) * mm, "end": v(1.72, 11.49) * mm});
            skLineSegment(sketch, "E381", {"start": v(1.72, 11.49) * mm, "end": v(1.41, 11.49) * mm});
            skLineSegment(sketch, "E382", {"start": v(1.41, 11.49) * mm, "end": v(0.94, 11.7) * mm});
            skLineSegment(sketch, "E383", {"start": v(0.94, 11.7) * mm, "end": v(0.4, 12.1) * mm});
            skLineSegment(sketch, "E384", {"start": v(0.4, 12.1) * mm, "end": v(0.22, 12.24) * mm});
            skLineSegment(sketch, "E385", {"start": v(0.22, 12.24) * mm, "end": v(-0.08, 12.55) * mm});
            skLineSegment(sketch, "E386", {"start": v(-0.08, 12.55) * mm, "end": v(-1.61, 14.09) * mm});
            skLineSegment(sketch, "E387", {"start": v(-1.61, 14.09) * mm, "end": v(-3.07, 15.68) * mm});
            skLineSegment(sketch, "E388", {"start": v(-3.07, 15.68) * mm, "end": v(-3.35, 16.01) * mm});
            skLineSegment(sketch, "E389", {"start": v(-3.35, 16.01) * mm, "end": v(-3.4, 16.31) * mm});
            skLineSegment(sketch, "E390", {"start": v(-3.4, 16.31) * mm, "end": v(-3.65, 17.2) * mm});
            skLineSegment(sketch, "E391", {"start": v(-3.65, 17.2) * mm, "end": v(-3.99, 17.9) * mm});
            skLineSegment(sketch, "E392", {"start": v(-3.99, 17.9) * mm, "end": v(-4.47, 18.4) * mm});
            skLineSegment(sketch, "E393", {"start": v(-4.47, 18.4) * mm, "end": v(-5.03, 18.89) * mm});
            skLineSegment(sketch, "E394", {"start": v(-5.03, 18.89) * mm, "end": v(-5.2, 19.05) * mm});
            skLineSegment(sketch, "E395", {"start": v(-5.2, 19.05) * mm, "end": v(-5.72, 19.67) * mm});
            skLineSegment(sketch, "E396", {"start": v(-5.72, 19.67) * mm, "end": v(-7.58, 21.25) * mm});
            skLineSegment(sketch, "E397", {"start": v(-7.58, 21.25) * mm, "end": v(-10.29, 22.82) * mm});
            skLineSegment(sketch, "E398", {"start": v(-10.29, 22.82) * mm, "end": v(-13.18, 23.95) * mm});
            skLineSegment(sketch, "E399", {"start": v(-13.18, 23.95) * mm, "end": v(-15.36, 24.63) * mm});
            skLineSegment(sketch, "E400", {"start": v(-15.36, 24.63) * mm, "end": v(-16.1, 24.85) * mm});
            skLineSegment(sketch, "E401", {"start": v(-16.1, 24.85) * mm, "end": v(-16.27, 24.92) * mm});
            skLineSegment(sketch, "E402", {"start": v(-16.27, 24.92) * mm, "end": v(-16.83, 25.05) * mm});
            skLineSegment(sketch, "E403", {"start": v(-16.83, 25.05) * mm, "end": v(-17.45, 24.96) * mm});
            skLineSegment(sketch, "E404", {"start": v(-17.45, 24.96) * mm, "end": v(-17.83, 24.52) * mm});
            skLineSegment(sketch, "E405", {"start": v(-17.83, 24.52) * mm, "end": v(-17.9, 23.88) * mm});
            skLineSegment(sketch, "E406", {"start": v(-17.9, 23.88) * mm, "end": v(-17.86, 23.68) * mm});
            skLineSegment(sketch, "E407", {"start": v(-17.86, 23.68) * mm, "end": v(-17.82, 23.54) * mm});
            skLineSegment(sketch, "E408", {"start": v(-17.82, 23.54) * mm, "end": v(-17.79, 23.1) * mm});
            skLineSegment(sketch, "E409", {"start": v(-17.79, 23.1) * mm, "end": v(-17.78, 22.24) * mm});
            skLineSegment(sketch, "E410", {"start": v(-17.78, 22.24) * mm, "end": v(-17.8, 21.11) * mm});
            skLineSegment(sketch, "E411", {"start": v(-17.8, 21.11) * mm, "end": v(-17.8, 20.11) * mm});
            skLineSegment(sketch, "E412", {"start": v(-17.8, 20.11) * mm, "end": v(-17.79, 19.78) * mm});
            skLineSegment(sketch, "E413", {"start": v(-17.79, 19.78) * mm, "end": v(-17.8, 19.63) * mm});
            skLineSegment(sketch, "E414", {"start": v(-17.8, 19.63) * mm, "end": v(-17.8, 19.17) * mm});
            skLineSegment(sketch, "E415", {"start": v(-17.8, 19.17) * mm, "end": v(-17.85, 18.58) * mm});
            skLineSegment(sketch, "E416", {"start": v(-17.85, 18.58) * mm, "end": v(-18.02, 18.19) * mm});
            skLineSegment(sketch, "E417", {"start": v(-18.02, 18.19) * mm, "end": v(-18.31, 18.12) * mm});
            skLineSegment(sketch, "E418", {"start": v(-18.31, 18.12) * mm, "end": v(-18.39, 18.15) * mm});
            skLineSegment(sketch, "E419", {"start": v(-18.39, 18.15) * mm, "end": v(-18.74, 18.28) * mm});
            skLineSegment(sketch, "E420", {"start": v(-18.74, 18.28) * mm, "end": v(-19.7, 18.93) * mm});
            skLineSegment(sketch, "E421", {"start": v(-19.7, 18.93) * mm, "end": v(-20.87, 20.13) * mm});
            skLineSegment(sketch, "E422", {"start": v(-20.87, 20.13) * mm, "end": v(-21.83, 21.61) * mm});
            skLineSegment(sketch, "E423", {"start": v(-21.83, 21.61) * mm, "end": v(-22.51, 23.23) * mm});
            skLineSegment(sketch, "E424", {"start": v(-22.51, 23.23) * mm, "end": v(-22.86, 24.83) * mm});
            skLineSegment(sketch, "E425", {"start": v(-22.86, 24.83) * mm, "end": v(-22.8, 26.28) * mm});
            skLineSegment(sketch, "E426", {"start": v(-22.8, 26.28) * mm, "end": v(-22.26, 27.42) * mm});
            skLineSegment(sketch, "E427", {"start": v(-22.26, 27.42) * mm, "end": v(-21.49, 28.03) * mm});
            skLineSegment(sketch, "E428", {"start": v(-21.49, 28.03) * mm, "end": v(-21.2, 28.12) * mm});
            skLineSegment(sketch, "E429", {"start": v(-21.2, 28.12) * mm, "end": v(-20.38, 28.38) * mm});
            skLineSegment(sketch, "E430", {"start": v(-20.38, 28.38) * mm, "end": v(-17.74, 28.6) * mm});
            skLineSegment(sketch, "E431", {"start": v(-17.74, 28.6) * mm, "end": v(-14.21, 28.11) * mm});
            skLineSegment(sketch, "E432", {"start": v(-14.21, 28.11) * mm, "end": v(-10.85, 26.98) * mm});
            skLineSegment(sketch, "E433", {"start": v(-10.85, 26.98) * mm, "end": v(-8.6, 25.94) * mm});
            skLineSegment(sketch, "E434", {"start": v(-8.6, 25.94) * mm, "end": v(-7.88, 25.54) * mm});
            skLineSegment(sketch, "E435", {"start": v(-7.88, 25.54) * mm, "end": v(-7.54, 25.36) * mm});
            skLineSegment(sketch, "E436", {"start": v(-7.54, 25.36) * mm, "end": v(-6.6, 24.68) * mm});
            skLineSegment(sketch, "E437", {"start": v(-6.6, 24.68) * mm, "end": v(-5.49, 23.6) * mm});
            skLineSegment(sketch, "E438", {"start": v(-5.49, 23.6) * mm, "end": v(-4.45, 22.44) * mm});
            skLineSegment(sketch, "E439", {"start": v(-4.45, 22.44) * mm, "end": v(-3.67, 21.59) * mm});
            skLineSegment(sketch, "E440", {"start": v(-3.67, 21.59) * mm, "end": v(-3.4, 21.32) * mm});
            skLineSegment(sketch, "E441", {"start": v(-3.4, 21.32) * mm, "end": v(-3.26, 21.14) * mm});
            skLineSegment(sketch, "E442", {"start": v(-3.26, 21.14) * mm, "end": v(-2.8, 20.65) * mm});
            skLineSegment(sketch, "E443", {"start": v(-2.8, 20.65) * mm, "end": v(-2.32, 20.27) * mm});
            skLineSegment(sketch, "E444", {"start": v(-2.32, 20.27) * mm, "end": v(-1.91, 20.09) * mm});
            skLineSegment(sketch, "E445", {"start": v(-1.91, 20.09) * mm, "end": v(-1.55, 20.02) * mm});
            skLineSegment(sketch, "E446", {"start": v(-1.55, 20.02) * mm, "end": v(-1.2, 19.97) * mm});
            skLineSegment(sketch, "E447", {"start": v(-1.2, 19.97) * mm, "end": v(-0.85, 19.86) * mm});
            skLineSegment(sketch, "E448", {"start": v(-0.85, 19.86) * mm, "end": v(-0.44, 19.6) * mm});
            skLineSegment(sketch, "E449", {"start": v(-0.44, 19.6) * mm, "end": v(-0.07, 19.23) * mm});
            skLineSegment(sketch, "E450", {"start": v(-0.07, 19.23) * mm, "end": v(0.04, 19.1) * mm});
            skLineSegment(sketch, "E451", {"start": v(0.04, 19.1) * mm, "end": v(0.28, 18.83) * mm});
            skLineSegment(sketch, "E452", {"start": v(0.28, 18.83) * mm, "end": v(1, 18) * mm});
            skLineSegment(sketch, "E453", {"start": v(1, 18) * mm, "end": v(1.85, 16.85) * mm});
            skLineSegment(sketch, "E454", {"start": v(1.85, 16.85) * mm, "end": v(2.54, 15.59) * mm});
            skLineSegment(sketch, "E455", {"start": v(2.54, 15.59) * mm, "end": v(2.92, 14.56) * mm});
            skLineSegment(sketch, "E456", {"start": v(2.92, 14.56) * mm, "end": v(3, 14.2) * mm});
            skLineSegment(sketch, "E457", {"start": v(3, 14.2) * mm, "end": v(3.07, 13.96) * mm});
            skLineSegment(sketch, "E458", {"start": v(3.07, 13.96) * mm, "end": v(3.26, 13.2) * mm});
            skLineSegment(sketch, "E459", {"start": v(3.26, 13.2) * mm, "end": v(3.3, 12.59) * mm});
            skLineSegment(sketch, "E460", {"start": v(3.3, 12.59) * mm, "end": v(3.22, 12.25) * mm});
            skLineSegment(sketch, "E461", {"start": v(3.22, 12.25) * mm, "end": v(3.07, 12.09) * mm});
            skLineSegment(sketch, "E462", {"start": v(3.07, 12.09) * mm, "end": v(2.94, 12.01) * mm});
            skLineSegment(sketch, "E463", {"start": v(2.94, 12.01) * mm, "end": v(2.9, 11.92) * mm});
            skLineSegment(sketch, "E464", {"start": v(2.9, 11.92) * mm, "end": v(3.03, 11.71) * mm});
            skLineSegment(sketch, "E465", {"start": v(3.03, 11.71) * mm, "end": v(3.32, 11.39) * mm});
            skLineSegment(sketch, "E466", {"start": v(3.32, 11.39) * mm, "end": v(3.42, 11.28) * mm});
            skLineSegment(sketch, "E467", {"start": v(3.42, 11.28) * mm, "end": v(3.58, 11.04) * mm});
            skLineSegment(sketch, "E468", {"start": v(3.58, 11.04) * mm, "end": v(4.08, 10.3) * mm});
            skLineSegment(sketch, "E469", {"start": v(4.08, 10.3) * mm, "end": v(4.56, 9.64) * mm});
            skLineSegment(sketch, "E470", {"start": v(4.56, 9.64) * mm, "end": v(5.08, 9.13) * mm});
            skLineSegment(sketch, "E471", {"start": v(5.08, 9.13) * mm, "end": v(5.66, 8.71) * mm});
            skLineSegment(sketch, "E472", {"start": v(5.66, 8.71) * mm, "end": v(5.86, 8.58) * mm});
            skLineSegment(sketch, "E473", {"start": v(5.86, 8.58) * mm, "end": v(6.2, 8.38) * mm});
            skLineSegment(sketch, "E474", {"start": v(6.2, 8.38) * mm, "end": v(7.18, 7.7) * mm});
            skLineSegment(sketch, "E475", {"start": v(7.18, 7.7) * mm, "end": v(7.79, 7.18) * mm});
            skLineSegment(sketch, "E476", {"start": v(7.79, 7.18) * mm, "end": v(7.68, 7.1) * mm});
            skLineSegment(sketch, "E477", {"start": v(7.68, 7.1) * mm, "end": v(7.06, 7.41) * mm});
            skLineSegment(sketch, "E478", {"start": v(7.06, 7.41) * mm, "end": v(6.87, 7.53) * mm});
            skLineSegment(sketch, "E479", {"start": v(6.87, 7.53) * mm, "end": v(6.71, 7.63) * mm});
            skLineSegment(sketch, "E480", {"start": v(6.71, 7.63) * mm, "end": v(6.22, 7.89) * mm});
            skLineSegment(sketch, "E481", {"start": v(6.22, 7.89) * mm, "end": v(6.1, 7.85) * mm});
            skLineSegment(sketch, "E482", {"start": v(6.1, 7.85) * mm, "end": v(6.36, 7.56) * mm});
            skLineSegment(sketch, "E483", {"start": v(6.36, 7.56) * mm, "end": v(6.8, 7.13) * mm});
            skLineSegment(sketch, "E484", {"start": v(6.8, 7.13) * mm, "end": v(7.26, 6.69) * mm});
            skLineSegment(sketch, "E485", {"start": v(7.26, 6.69) * mm, "end": v(7.56, 6.36) * mm});
            skLineSegment(sketch, "E486", {"start": v(7.56, 6.36) * mm, "end": v(7.52, 6.26) * mm});
            skLineSegment(sketch, "E487", {"start": v(7.52, 6.26) * mm, "end": v(7.11, 6.45) * mm});
            skLineSegment(sketch, "E488", {"start": v(7.11, 6.45) * mm, "end": v(6.98, 6.52) * mm});
            skLineSegment(sketch, "E489", {"start": v(6.98, 6.52) * mm, "end": v(6.61, 6.78) * mm});
            skLineSegment(sketch, "E490", {"start": v(6.61, 6.78) * mm, "end": v(5.52, 7.61) * mm});
            skLineSegment(sketch, "E491", {"start": v(5.52, 7.61) * mm, "end": v(4.66, 8.4) * mm});
            skLineSegment(sketch, "E492", {"start": v(4.66, 8.4) * mm, "end": v(4.08, 9.09) * mm});
            skLineSegment(sketch, "E493", {"start": v(4.08, 9.09) * mm, "end": v(3.64, 9.67) * mm});
            skLineSegment(sketch, "E494", {"start": v(3.64, 9.67) * mm, "end": v(3.48, 9.86) * mm});
            skLineSegment(sketch, "E495.bottom", {"start": v(-3.86, 57.2) * mm, "end": v(3.86, 57.2) * mm});
            skLineSegment(sketch, "E495.top", {"start": v(-3.86, 49.48) * mm, "end": v(3.86, 49.48) * mm});
            skLineSegment(sketch, "E495.left", {"start": v(-3.86, 57.2) * mm, "end": v(-3.86, 49.48) * mm});
            skLineSegment(sketch, "E495.right", {"start": v(3.86, 57.2) * mm, "end": v(3.86, 49.48) * mm});
            skLineSegment(sketch, "E496.bottom", {"start": v(3.86, -57.2) * mm, "end": v(-3.86, -57.2) * mm});
            skLineSegment(sketch, "E496.top", {"start": v(3.86, -49.48) * mm, "end": v(-3.86, -49.48) * mm});
            skLineSegment(sketch, "E496.left", {"start": v(3.86, -57.2) * mm, "end": v(3.86, -49.48) * mm});
            skLineSegment(sketch, "E496.right", {"start": v(-3.86, -57.2) * mm, "end": v(-3.86, -49.48) * mm});
            skCircle(sketch, "E497", {"center": v(0, 30.43) * mm, "radius": 4.95 * mm});
            skCircle(sketch, "E498", {"center": v(0, 41.86) * mm, "radius": 2.54 * mm});
            skLineSegment(sketch, "E499", {"start": v(2.54, 41.79) * mm, "end": v(2.54, 34.68) * mm});
            skLineSegment(sketch, "E500", {"start": v(-2.54, 41.78) * mm, "end": v(-2.54, 34.68) * mm});
            skCircle(sketch, "E501", {"center": v(0, -39.42) * mm, "radius": 4.95 * mm});
            skCircle(sketch, "E502", {"center": v(0, -28) * mm, "radius": 2.54 * mm});
            skLineSegment(sketch, "E503", {"start": v(3, -14.34) * mm, "end": v(3.03, -14.76) * mm});
            skLineSegment(sketch, "E504", {"start": v(-2.54, -28) * mm, "end": v(-2.54, -35.17) * mm});
            skLineSegment(sketch, "E505", {"start": v(2.54, -27.97) * mm, "end": v(2.54, -35.17) * mm});
            skLineSegment(sketch, "E506.bottom", {"start": v(-3.86, 57.2) * mm, "end": v(3.91, 57.2) * mm});
            skLineSegment(sketch, "E507.left", {"start": v(-3.86, 49.48) * mm, "end": v(-3.86, 53.37) * mm});
            skLineSegment(sketch, "E507.right", {"start": v(3.86, 49.48) * mm, "end": v(3.86, 53.34) * mm});
            skSolve(sketch);
        }
        {
            var Q0;
            Q0=makeQuery(id+"F0.imprint","IMPRINT",FACE,{"disambiguationData":[TD([[makeQuery(id+"F0.imprint","IMPRINT",EDGE,{"derivedFrom":sQuery(id+"F0.wireOp",EDGE,"E0.bottom")}),1.0]])]});
            extrude(context, id + "F1", {"entities" : qUnion([Q0]), "depth" : 9.52 * mm, "offsetDistance" : 25.4 * mm});
        }
        {
            var Q0;
            Q0=makeQuery(id+"F0.imprint","IMPRINT",FACE,{"disambiguationData":[TD([[makeQuery(id+"F0.imprint","IMPRINT",EDGE,{"derivedFrom":sQuery(id+"F0.wireOp",EDGE,"E6")}),-1.0]])]});
            var Q1;
            Q1=makeQuery(id+"F0.imprint","IMPRINT",FACE,{"disambiguationData":[TD([[makeQuery(id+"F0.imprint","IMPRINT",EDGE,{"derivedFrom":sQuery(id+"F0.wireOp",EDGE,"E307")}),-1.0]])]});
            var Q2;
            Q2=makeQuery(id+"F0.imprint","IMPRINT",FACE,{"disambiguationData":[TD([[makeQuery(id+"F0.imprint","IMPRINT",EDGE,{"derivedFrom":sQuery(id+"F0.wireOp",EDGE,"E375")}),-1.0]])]});
            var Q3;
            Q3=makeQuery(id+"F0.imprint","IMPRINT",FACE,{"disambiguationData":[TD([[makeQuery(id+"F0.imprint","IMPRINT",EDGE,{"derivedFrom":sQuery(id+"F0.wireOp",EDGE,"E255")}),-1.0]])]});
            var Q4;
            Q4=makeQuery(id+"F0.imprint","IMPRINT",FACE,{"disambiguationData":[TD([[makeQuery(id+"F0.imprint","IMPRINT",EDGE,{"derivedFrom":sQuery(id+"F0.wireOp",EDGE,"E101")}),-1.0]])]});
            var Q5;
            Q5=makeQuery(id+"F0.imprint","IMPRINT",FACE,{"disambiguationData":[TD([[makeQuery(id+"F0.imprint","IMPRINT",EDGE,{"derivedFrom":sQuery(id+"F0.wireOp",EDGE,"E79")}),-1.0]])]});
            var Q6;
            Q6=makeQuery(id+"F0.imprint","IMPRINT",FACE,{"disambiguationData":[TD([[makeQuery(id+"F0.imprint","IMPRINT",EDGE,{"derivedFrom":sQuery(id+"F0.wireOp",EDGE,"E173")}),-1.0]])]});
            extrude(context, id + "F2", {"entities" : qUnion([Q0, Q1, Q2, Q3, Q4, Q5, Q6]), "operationType" : NewBodyOperationType.ADD, "depth" : 8.76 * mm, "offsetDistance" : 25.4 * mm});
        }
        {
            var Q0;
            Q0=makeQuery(id+"F1.opExtrude","SWEPT_BODY",BODY,{"disambiguationData":[OSD([sQuery(id+"F0.wireOp",EDGE,"E0.bottom"),sQuery(id+"F0.wireOp",EDGE,"E0.top"),sQuery(id+"F0.wireOp",EDGE,"E1.left"),sQuery(id+"F0.wireOp",EDGE,"E1.right"),sQuery(id+"F0.wireOp",EDGE,"E2"),sQuery(id+"F0.wireOp",EDGE,"E3"),sQuery(id+"F0.wireOp",EDGE,"E4"),sQuery(id+"F0.wireOp",EDGE,"E5"),sQuery(id+"F0.wireOp",EDGE,"E6"),sQuery(id+"F0.wireOp",EDGE,"E7"),sQuery(id+"F0.wireOp",EDGE,"E8"),sQuery(id+"F0.wireOp",EDGE,"E9"),sQuery(id+"F0.wireOp",EDGE,"E10"),sQuery(id+"F0.wireOp",EDGE,"E11"),sQuery(id+"F0.wireOp",EDGE,"E12"),sQuery(id+"F0.wireOp",EDGE,"E13"),sQuery(id+"F0.wireOp",EDGE,"E14"),sQuery(id+"F0.wireOp",EDGE,"E15"),sQuery(id+"F0.wireOp",EDGE,"E16"),sQuery(id+"F0.wireOp",EDGE,"E17"),sQuery(id+"F0.wireOp",EDGE,"E18"),sQuery(id+"F0.wireOp",EDGE,"E19"),sQuery(id+"F0.wireOp",EDGE,"E20"),sQuery(id+"F0.wireOp",EDGE,"E21"),sQuery(id+"F0.wireOp",EDGE,"E22"),sQuery(id+"F0.wireOp",EDGE,"E23"),sQuery(id+"F0.wireOp",EDGE,"E24"),sQuery(id+"F0.wireOp",EDGE,"E25"),sQuery(id+"F0.wireOp",EDGE,"E26"),sQuery(id+"F0.wireOp",EDGE,"E27"),sQuery(id+"F0.wireOp",EDGE,"E28"),sQuery(id+"F0.wireOp",EDGE,"E29"),sQuery(id+"F0.wireOp",EDGE,"E30"),sQuery(id+"F0.wireOp",EDGE,"E31"),sQuery(id+"F0.wireOp",EDGE,"E32"),sQuery(id+"F0.wireOp",EDGE,"E33"),sQuery(id+"F0.wireOp",EDGE,"E34"),sQuery(id+"F0.wireOp",EDGE,"E35"),sQuery(id+"F0.wireOp",EDGE,"E36"),sQuery(id+"F0.wireOp",EDGE,"E37"),sQuery(id+"F0.wireOp",EDGE,"E38"),sQuery(id+"F0.wireOp",EDGE,"E39"),sQuery(id+"F0.wireOp",EDGE,"E40"),sQuery(id+"F0.wireOp",EDGE,"E41"),sQuery(id+"F0.wireOp",EDGE,"E42"),sQuery(id+"F0.wireOp",EDGE,"E43"),sQuery(id+"F0.wireOp",EDGE,"E44"),sQuery(id+"F0.wireOp",EDGE,"E45"),sQuery(id+"F0.wireOp",EDGE,"E46"),sQuery(id+"F0.wireOp",EDGE,"E47"),sQuery(id+"F0.wireOp",EDGE,"E48"),sQuery(id+"F0.wireOp",EDGE,"E49"),sQuery(id+"F0.wireOp",EDGE,"E50"),sQuery(id+"F0.wireOp",EDGE,"E51"),sQuery(id+"F0.wireOp",EDGE,"E52"),sQuery(id+"F0.wireOp",EDGE,"E53"),sQuery(id+"F0.wireOp",EDGE,"E54"),sQuery(id+"F0.wireOp",EDGE,"E55"),sQuery(id+"F0.wireOp",EDGE,"E56"),sQuery(id+"F0.wireOp",EDGE,"E57"),sQuery(id+"F0.wireOp",EDGE,"E58"),sQuery(id+"F0.wireOp",EDGE,"E59"),sQuery(id+"F0.wireOp",EDGE,"E60"),sQuery(id+"F0.wireOp",EDGE,"E61"),sQuery(id+"F0.wireOp",EDGE,"E62"),sQuery(id+"F0.wireOp",EDGE,"E63"),sQuery(id+"F0.wireOp",EDGE,"E64"),sQuery(id+"F0.wireOp",EDGE,"E65"),sQuery(id+"F0.wireOp",EDGE,"E66"),sQuery(id+"F0.wireOp",EDGE,"E67"),sQuery(id+"F0.wireOp",EDGE,"E68"),sQuery(id+"F0.wireOp",EDGE,"E69"),sQuery(id+"F0.wireOp",EDGE,"E70"),sQuery(id+"F0.wireOp",EDGE,"E71"),sQuery(id+"F0.wireOp",EDGE,"E72"),sQuery(id+"F0.wireOp",EDGE,"E73"),sQuery(id+"F0.wireOp",EDGE,"E74"),sQuery(id+"F0.wireOp",EDGE,"E75"),sQuery(id+"F0.wireOp",EDGE,"E76"),sQuery(id+"F0.wireOp",EDGE,"E77"),sQuery(id+"F0.wireOp",EDGE,"E78"),sQuery(id+"F0.wireOp",EDGE,"E79"),sQuery(id+"F0.wireOp",EDGE,"E80"),sQuery(id+"F0.wireOp",EDGE,"E81"),sQuery(id+"F0.wireOp",EDGE,"E82"),sQuery(id+"F0.wireOp",EDGE,"E83"),sQuery(id+"F0.wireOp",EDGE,"E84"),sQuery(id+"F0.wireOp",EDGE,"E85"),sQuery(id+"F0.wireOp",EDGE,"E86"),sQuery(id+"F0.wireOp",EDGE,"E87"),sQuery(id+"F0.wireOp",EDGE,"E88"),sQuery(id+"F0.wireOp",EDGE,"E89"),sQuery(id+"F0.wireOp",EDGE,"E90"),sQuery(id+"F0.wireOp",EDGE,"E91"),sQuery(id+"F0.wireOp",EDGE,"E92"),sQuery(id+"F0.wireOp",EDGE,"E93"),sQuery(id+"F0.wireOp",EDGE,"E94"),sQuery(id+"F0.wireOp",EDGE,"E95"),sQuery(id+"F0.wireOp",EDGE,"E96"),sQuery(id+"F0.wireOp",EDGE,"E97"),sQuery(id+"F0.wireOp",EDGE,"E98"),sQuery(id+"F0.wireOp",EDGE,"E99"),sQuery(id+"F0.wireOp",EDGE,"E100"),sQuery(id+"F0.wireOp",EDGE,"E101"),sQuery(id+"F0.wireOp",EDGE,"E102"),sQuery(id+"F0.wireOp",EDGE,"E103"),sQuery(id+"F0.wireOp",EDGE,"E104"),sQuery(id+"F0.wireOp",EDGE,"E105"),sQuery(id+"F0.wireOp",EDGE,"E106"),sQuery(id+"F0.wireOp",EDGE,"E107"),sQuery(id+"F0.wireOp",EDGE,"E108"),sQuery(id+"F0.wireOp",EDGE,"E109"),sQuery(id+"F0.wireOp",EDGE,"E110"),sQuery(id+"F0.wireOp",EDGE,"E111"),sQuery(id+"F0.wireOp",EDGE,"E112"),sQuery(id+"F0.wireOp",EDGE,"E113"),sQuery(id+"F0.wireOp",EDGE,"E114"),sQuery(id+"F0.wireOp",EDGE,"E115"),sQuery(id+"F0.wireOp",EDGE,"E116"),sQuery(id+"F0.wireOp",EDGE,"E117"),sQuery(id+"F0.wireOp",EDGE,"E118"),sQuery(id+"F0.wireOp",EDGE,"E119"),sQuery(id+"F0.wireOp",EDGE,"E120"),sQuery(id+"F0.wireOp",EDGE,"E121"),sQuery(id+"F0.wireOp",EDGE,"E122"),sQuery(id+"F0.wireOp",EDGE,"E123"),sQuery(id+"F0.wireOp",EDGE,"E124"),sQuery(id+"F0.wireOp",EDGE,"E125"),sQuery(id+"F0.wireOp",EDGE,"E126"),sQuery(id+"F0.wireOp",EDGE,"E127"),sQuery(id+"F0.wireOp",EDGE,"E128"),sQuery(id+"F0.wireOp",EDGE,"E129"),sQuery(id+"F0.wireOp",EDGE,"E130"),sQuery(id+"F0.wireOp",EDGE,"E131"),sQuery(id+"F0.wireOp",EDGE,"E132"),sQuery(id+"F0.wireOp",EDGE,"E133"),sQuery(id+"F0.wireOp",EDGE,"E134"),sQuery(id+"F0.wireOp",EDGE,"E135"),sQuery(id+"F0.wireOp",EDGE,"E136"),sQuery(id+"F0.wireOp",EDGE,"E137"),sQuery(id+"F0.wireOp",EDGE,"E138"),sQuery(id+"F0.wireOp",EDGE,"E139"),sQuery(id+"F0.wireOp",EDGE,"E140"),sQuery(id+"F0.wireOp",EDGE,"E141"),sQuery(id+"F0.wireOp",EDGE,"E142"),sQuery(id+"F0.wireOp",EDGE,"E143"),sQuery(id+"F0.wireOp",EDGE,"E144"),sQuery(id+"F0.wireOp",EDGE,"E145"),sQuery(id+"F0.wireOp",EDGE,"E146"),sQuery(id+"F0.wireOp",EDGE,"E147"),sQuery(id+"F0.wireOp",EDGE,"E148"),sQuery(id+"F0.wireOp",EDGE,"E149"),sQuery(id+"F0.wireOp",EDGE,"E150"),sQuery(id+"F0.wireOp",EDGE,"E151"),sQuery(id+"F0.wireOp",EDGE,"E152"),sQuery(id+"F0.wireOp",EDGE,"E153"),sQuery(id+"F0.wireOp",EDGE,"E154"),sQuery(id+"F0.wireOp",EDGE,"E155"),sQuery(id+"F0.wireOp",EDGE,"E156"),sQuery(id+"F0.wireOp",EDGE,"E157"),sQuery(id+"F0.wireOp",EDGE,"E158"),sQuery(id+"F0.wireOp",EDGE,"E159"),sQuery(id+"F0.wireOp",EDGE,"E160"),sQuery(id+"F0.wireOp",EDGE,"E161"),sQuery(id+"F0.wireOp",EDGE,"E162"),sQuery(id+"F0.wireOp",EDGE,"E163"),sQuery(id+"F0.wireOp",EDGE,"E164"),sQuery(id+"F0.wireOp",EDGE,"E165"),sQuery(id+"F0.wireOp",EDGE,"E166"),sQuery(id+"F0.wireOp",EDGE,"E167"),sQuery(id+"F0.wireOp",EDGE,"E168"),sQuery(id+"F0.wireOp",EDGE,"E169"),sQuery(id+"F0.wireOp",EDGE,"E170"),sQuery(id+"F0.wireOp",EDGE,"E171"),sQuery(id+"F0.wireOp",EDGE,"E172"),sQuery(id+"F0.wireOp",EDGE,"E173"),sQuery(id+"F0.wireOp",EDGE,"E174"),sQuery(id+"F0.wireOp",EDGE,"E175"),sQuery(id+"F0.wireOp",EDGE,"E176"),sQuery(id+"F0.wireOp",EDGE,"E177"),sQuery(id+"F0.wireOp",EDGE,"E178"),sQuery(id+"F0.wireOp",EDGE,"E179"),sQuery(id+"F0.wireOp",EDGE,"E180"),sQuery(id+"F0.wireOp",EDGE,"E181"),sQuery(id+"F0.wireOp",EDGE,"E182"),sQuery(id+"F0.wireOp",EDGE,"E183"),sQuery(id+"F0.wireOp",EDGE,"E184"),sQuery(id+"F0.wireOp",EDGE,"E185"),sQuery(id+"F0.wireOp",EDGE,"E186"),sQuery(id+"F0.wireOp",EDGE,"E187"),sQuery(id+"F0.wireOp",EDGE,"E188"),sQuery(id+"F0.wireOp",EDGE,"E189"),sQuery(id+"F0.wireOp",EDGE,"E190"),sQuery(id+"F0.wireOp",EDGE,"E191"),sQuery(id+"F0.wireOp",EDGE,"E192"),sQuery(id+"F0.wireOp",EDGE,"E193"),sQuery(id+"F0.wireOp",EDGE,"E194"),sQuery(id+"F0.wireOp",EDGE,"E195"),sQuery(id+"F0.wireOp",EDGE,"E196"),sQuery(id+"F0.wireOp",EDGE,"E197"),sQuery(id+"F0.wireOp",EDGE,"E198"),sQuery(id+"F0.wireOp",EDGE,"E199"),sQuery(id+"F0.wireOp",EDGE,"E200"),sQuery(id+"F0.wireOp",EDGE,"E201"),sQuery(id+"F0.wireOp",EDGE,"E202"),sQuery(id+"F0.wireOp",EDGE,"E203"),sQuery(id+"F0.wireOp",EDGE,"E204"),sQuery(id+"F0.wireOp",EDGE,"E205"),sQuery(id+"F0.wireOp",EDGE,"E206"),sQuery(id+"F0.wireOp",EDGE,"E207"),sQuery(id+"F0.wireOp",EDGE,"E208"),sQuery(id+"F0.wireOp",EDGE,"E209"),sQuery(id+"F0.wireOp",EDGE,"E210"),sQuery(id+"F0.wireOp",EDGE,"E211"),sQuery(id+"F0.wireOp",EDGE,"E212"),sQuery(id+"F0.wireOp",EDGE,"E213"),sQuery(id+"F0.wireOp",EDGE,"E214"),sQuery(id+"F0.wireOp",EDGE,"E215"),sQuery(id+"F0.wireOp",EDGE,"E216"),sQuery(id+"F0.wireOp",EDGE,"E217"),sQuery(id+"F0.wireOp",EDGE,"E218"),sQuery(id+"F0.wireOp",EDGE,"E219"),sQuery(id+"F0.wireOp",EDGE,"E220"),sQuery(id+"F0.wireOp",EDGE,"E221"),sQuery(id+"F0.wireOp",EDGE,"E222"),sQuery(id+"F0.wireOp",EDGE,"E223"),sQuery(id+"F0.wireOp",EDGE,"E224"),sQuery(id+"F0.wireOp",EDGE,"E225"),sQuery(id+"F0.wireOp",EDGE,"E226"),sQuery(id+"F0.wireOp",EDGE,"E227"),sQuery(id+"F0.wireOp",EDGE,"E228"),sQuery(id+"F0.wireOp",EDGE,"E229"),sQuery(id+"F0.wireOp",EDGE,"E230"),sQuery(id+"F0.wireOp",EDGE,"E231"),sQuery(id+"F0.wireOp",EDGE,"E232"),sQuery(id+"F0.wireOp",EDGE,"E233"),sQuery(id+"F0.wireOp",EDGE,"E234"),sQuery(id+"F0.wireOp",EDGE,"E235"),sQuery(id+"F0.wireOp",EDGE,"E236"),sQuery(id+"F0.wireOp",EDGE,"E237"),sQuery(id+"F0.wireOp",EDGE,"E238"),sQuery(id+"F0.wireOp",EDGE,"E239"),sQuery(id+"F0.wireOp",EDGE,"E240"),sQuery(id+"F0.wireOp",EDGE,"E241"),sQuery(id+"F0.wireOp",EDGE,"E242"),sQuery(id+"F0.wireOp",EDGE,"E243"),sQuery(id+"F0.wireOp",EDGE,"E244"),sQuery(id+"F0.wireOp",EDGE,"E245"),sQuery(id+"F0.wireOp",EDGE,"E246"),sQuery(id+"F0.wireOp",EDGE,"E247"),sQuery(id+"F0.wireOp",EDGE,"E248"),sQuery(id+"F0.wireOp",EDGE,"E249"),sQuery(id+"F0.wireOp",EDGE,"E250"),sQuery(id+"F0.wireOp",EDGE,"E251"),sQuery(id+"F0.wireOp",EDGE,"E252"),sQuery(id+"F0.wireOp",EDGE,"E253"),sQuery(id+"F0.wireOp",EDGE,"E254"),sQuery(id+"F0.wireOp",EDGE,"E255"),sQuery(id+"F0.wireOp",EDGE,"E256"),sQuery(id+"F0.wireOp",EDGE,"E257"),sQuery(id+"F0.wireOp",EDGE,"E258"),sQuery(id+"F0.wireOp",EDGE,"E259"),sQuery(id+"F0.wireOp",EDGE,"E260"),sQuery(id+"F0.wireOp",EDGE,"E261"),sQuery(id+"F0.wireOp",EDGE,"E262"),sQuery(id+"F0.wireOp",EDGE,"E263"),sQuery(id+"F0.wireOp",EDGE,"E264"),sQuery(id+"F0.wireOp",EDGE,"E265"),sQuery(id+"F0.wireOp",EDGE,"E266"),sQuery(id+"F0.wireOp",EDGE,"E267"),sQuery(id+"F0.wireOp",EDGE,"E268"),sQuery(id+"F0.wireOp",EDGE,"E269"),sQuery(id+"F0.wireOp",EDGE,"E270"),sQuery(id+"F0.wireOp",EDGE,"E271"),sQuery(id+"F0.wireOp",EDGE,"E272"),sQuery(id+"F0.wireOp",EDGE,"E273"),sQuery(id+"F0.wireOp",EDGE,"E274"),sQuery(id+"F0.wireOp",EDGE,"E275"),sQuery(id+"F0.wireOp",EDGE,"E276"),sQuery(id+"F0.wireOp",EDGE,"E277"),sQuery(id+"F0.wireOp",EDGE,"E278"),sQuery(id+"F0.wireOp",EDGE,"E279"),sQuery(id+"F0.wireOp",EDGE,"E280"),sQuery(id+"F0.wireOp",EDGE,"E281"),sQuery(id+"F0.wireOp",EDGE,"E282"),sQuery(id+"F0.wireOp",EDGE,"E283"),sQuery(id+"F0.wireOp",EDGE,"E284"),sQuery(id+"F0.wireOp",EDGE,"E285"),sQuery(id+"F0.wireOp",EDGE,"E286"),sQuery(id+"F0.wireOp",EDGE,"E287"),sQuery(id+"F0.wireOp",EDGE,"E288"),sQuery(id+"F0.wireOp",EDGE,"E289"),sQuery(id+"F0.wireOp",EDGE,"E290"),sQuery(id+"F0.wireOp",EDGE,"E291"),sQuery(id+"F0.wireOp",EDGE,"E292"),sQuery(id+"F0.wireOp",EDGE,"E293"),sQuery(id+"F0.wireOp",EDGE,"E294"),sQuery(id+"F0.wireOp",EDGE,"E295"),sQuery(id+"F0.wireOp",EDGE,"E296"),sQuery(id+"F0.wireOp",EDGE,"E297"),sQuery(id+"F0.wireOp",EDGE,"E298"),sQuery(id+"F0.wireOp",EDGE,"E299"),sQuery(id+"F0.wireOp",EDGE,"E300"),sQuery(id+"F0.wireOp",EDGE,"E301"),sQuery(id+"F0.wireOp",EDGE,"E302"),sQuery(id+"F0.wireOp",EDGE,"E303"),sQuery(id+"F0.wireOp",EDGE,"E304"),sQuery(id+"F0.wireOp",EDGE,"E305"),sQuery(id+"F0.wireOp",EDGE,"E306"),sQuery(id+"F0.wireOp",EDGE,"E307"),sQuery(id+"F0.wireOp",EDGE,"E308"),sQuery(id+"F0.wireOp",EDGE,"E309"),sQuery(id+"F0.wireOp",EDGE,"E310"),sQuery(id+"F0.wireOp",EDGE,"E311"),sQuery(id+"F0.wireOp",EDGE,"E312"),sQuery(id+"F0.wireOp",EDGE,"E313"),sQuery(id+"F0.wireOp",EDGE,"E314"),sQuery(id+"F0.wireOp",EDGE,"E315"),sQuery(id+"F0.wireOp",EDGE,"E316"),sQuery(id+"F0.wireOp",EDGE,"E317"),sQuery(id+"F0.wireOp",EDGE,"E318"),sQuery(id+"F0.wireOp",EDGE,"E319"),sQuery(id+"F0.wireOp",EDGE,"E320"),sQuery(id+"F0.wireOp",EDGE,"E321"),sQuery(id+"F0.wireOp",EDGE,"E322"),sQuery(id+"F0.wireOp",EDGE,"E323"),sQuery(id+"F0.wireOp",EDGE,"E324"),sQuery(id+"F0.wireOp",EDGE,"E325"),sQuery(id+"F0.wireOp",EDGE,"E326"),sQuery(id+"F0.wireOp",EDGE,"E327"),sQuery(id+"F0.wireOp",EDGE,"E328"),sQuery(id+"F0.wireOp",EDGE,"E329"),sQuery(id+"F0.wireOp",EDGE,"E330"),sQuery(id+"F0.wireOp",EDGE,"E331"),sQuery(id+"F0.wireOp",EDGE,"E332"),sQuery(id+"F0.wireOp",EDGE,"E333"),sQuery(id+"F0.wireOp",EDGE,"E334"),sQuery(id+"F0.wireOp",EDGE,"E335"),sQuery(id+"F0.wireOp",EDGE,"E336"),sQuery(id+"F0.wireOp",EDGE,"E337"),sQuery(id+"F0.wireOp",EDGE,"E338"),sQuery(id+"F0.wireOp",EDGE,"E339"),sQuery(id+"F0.wireOp",EDGE,"E340"),sQuery(id+"F0.wireOp",EDGE,"E341"),sQuery(id+"F0.wireOp",EDGE,"E342"),sQuery(id+"F0.wireOp",EDGE,"E343"),sQuery(id+"F0.wireOp",EDGE,"E344"),sQuery(id+"F0.wireOp",EDGE,"E345"),sQuery(id+"F0.wireOp",EDGE,"E346"),sQuery(id+"F0.wireOp",EDGE,"E347"),sQuery(id+"F0.wireOp",EDGE,"E348"),sQuery(id+"F0.wireOp",EDGE,"E349"),sQuery(id+"F0.wireOp",EDGE,"E350"),sQuery(id+"F0.wireOp",EDGE,"E351"),sQuery(id+"F0.wireOp",EDGE,"E352"),sQuery(id+"F0.wireOp",EDGE,"E353"),sQuery(id+"F0.wireOp",EDGE,"E354"),sQuery(id+"F0.wireOp",EDGE,"E355"),sQuery(id+"F0.wireOp",EDGE,"E356"),sQuery(id+"F0.wireOp",EDGE,"E357"),sQuery(id+"F0.wireOp",EDGE,"E358"),sQuery(id+"F0.wireOp",EDGE,"E359"),sQuery(id+"F0.wireOp",EDGE,"E360"),sQuery(id+"F0.wireOp",EDGE,"E361"),sQuery(id+"F0.wireOp",EDGE,"E362"),sQuery(id+"F0.wireOp",EDGE,"E363"),sQuery(id+"F0.wireOp",EDGE,"E364"),sQuery(id+"F0.wireOp",EDGE,"E365"),sQuery(id+"F0.wireOp",EDGE,"E366"),sQuery(id+"F0.wireOp",EDGE,"E367"),sQuery(id+"F0.wireOp",EDGE,"E368"),sQuery(id+"F0.wireOp",EDGE,"E369"),sQuery(id+"F0.wireOp",EDGE,"E370"),sQuery(id+"F0.wireOp",EDGE,"E371"),sQuery(id+"F0.wireOp",EDGE,"E372"),sQuery(id+"F0.wireOp",EDGE,"E373"),sQuery(id+"F0.wireOp",EDGE,"E374"),sQuery(id+"F0.wireOp",EDGE,"E375"),sQuery(id+"F0.wireOp",EDGE,"E376"),sQuery(id+"F0.wireOp",EDGE,"E377"),sQuery(id+"F0.wireOp",EDGE,"E378"),sQuery(id+"F0.wireOp",EDGE,"E379"),sQuery(id+"F0.wireOp",EDGE,"E380"),sQuery(id+"F0.wireOp",EDGE,"E381"),sQuery(id+"F0.wireOp",EDGE,"E382"),sQuery(id+"F0.wireOp",EDGE,"E383"),sQuery(id+"F0.wireOp",EDGE,"E384"),sQuery(id+"F0.wireOp",EDGE,"E385"),sQuery(id+"F0.wireOp",EDGE,"E386"),sQuery(id+"F0.wireOp",EDGE,"E387"),sQuery(id+"F0.wireOp",EDGE,"E388"),sQuery(id+"F0.wireOp",EDGE,"E389"),sQuery(id+"F0.wireOp",EDGE,"E390"),sQuery(id+"F0.wireOp",EDGE,"E391"),sQuery(id+"F0.wireOp",EDGE,"E392"),sQuery(id+"F0.wireOp",EDGE,"E393"),sQuery(id+"F0.wireOp",EDGE,"E394"),sQuery(id+"F0.wireOp",EDGE,"E395"),sQuery(id+"F0.wireOp",EDGE,"E396"),sQuery(id+"F0.wireOp",EDGE,"E397"),sQuery(id+"F0.wireOp",EDGE,"E398"),sQuery(id+"F0.wireOp",EDGE,"E399"),sQuery(id+"F0.wireOp",EDGE,"E400"),sQuery(id+"F0.wireOp",EDGE,"E401"),sQuery(id+"F0.wireOp",EDGE,"E402"),sQuery(id+"F0.wireOp",EDGE,"E403"),sQuery(id+"F0.wireOp",EDGE,"E404"),sQuery(id+"F0.wireOp",EDGE,"E405"),sQuery(id+"F0.wireOp",EDGE,"E406"),sQuery(id+"F0.wireOp",EDGE,"E407"),sQuery(id+"F0.wireOp",EDGE,"E408"),sQuery(id+"F0.wireOp",EDGE,"E409"),sQuery(id+"F0.wireOp",EDGE,"E410"),sQuery(id+"F0.wireOp",EDGE,"E411"),sQuery(id+"F0.wireOp",EDGE,"E412"),sQuery(id+"F0.wireOp",EDGE,"E413"),sQuery(id+"F0.wireOp",EDGE,"E414"),sQuery(id+"F0.wireOp",EDGE,"E415"),sQuery(id+"F0.wireOp",EDGE,"E416"),sQuery(id+"F0.wireOp",EDGE,"E417"),sQuery(id+"F0.wireOp",EDGE,"E418"),sQuery(id+"F0.wireOp",EDGE,"E419"),sQuery(id+"F0.wireOp",EDGE,"E420"),sQuery(id+"F0.wireOp",EDGE,"E421"),sQuery(id+"F0.wireOp",EDGE,"E422"),sQuery(id+"F0.wireOp",EDGE,"E423"),sQuery(id+"F0.wireOp",EDGE,"E424"),sQuery(id+"F0.wireOp",EDGE,"E425"),sQuery(id+"F0.wireOp",EDGE,"E426"),sQuery(id+"F0.wireOp",EDGE,"E427"),sQuery(id+"F0.wireOp",EDGE,"E428"),sQuery(id+"F0.wireOp",EDGE,"E429"),sQuery(id+"F0.wireOp",EDGE,"E430"),sQuery(id+"F0.wireOp",EDGE,"E431"),sQuery(id+"F0.wireOp",EDGE,"E432"),sQuery(id+"F0.wireOp",EDGE,"E433"),sQuery(id+"F0.wireOp",EDGE,"E434"),sQuery(id+"F0.wireOp",EDGE,"E435"),sQuery(id+"F0.wireOp",EDGE,"E436"),sQuery(id+"F0.wireOp",EDGE,"E437"),sQuery(id+"F0.wireOp",EDGE,"E438"),sQuery(id+"F0.wireOp",EDGE,"E439"),sQuery(id+"F0.wireOp",EDGE,"E440"),sQuery(id+"F0.wireOp",EDGE,"E441"),sQuery(id+"F0.wireOp",EDGE,"E442"),sQuery(id+"F0.wireOp",EDGE,"E443"),sQuery(id+"F0.wireOp",EDGE,"E444"),sQuery(id+"F0.wireOp",EDGE,"E445"),sQuery(id+"F0.wireOp",EDGE,"E446"),sQuery(id+"F0.wireOp",EDGE,"E447"),sQuery(id+"F0.wireOp",EDGE,"E448"),sQuery(id+"F0.wireOp",EDGE,"E449"),sQuery(id+"F0.wireOp",EDGE,"E450"),sQuery(id+"F0.wireOp",EDGE,"E451"),sQuery(id+"F0.wireOp",EDGE,"E452"),sQuery(id+"F0.wireOp",EDGE,"E453"),sQuery(id+"F0.wireOp",EDGE,"E454"),sQuery(id+"F0.wireOp",EDGE,"E455"),sQuery(id+"F0.wireOp",EDGE,"E456"),sQuery(id+"F0.wireOp",EDGE,"E457"),sQuery(id+"F0.wireOp",EDGE,"E458"),sQuery(id+"F0.wireOp",EDGE,"E459"),sQuery(id+"F0.wireOp",EDGE,"E460"),sQuery(id+"F0.wireOp",EDGE,"E461"),sQuery(id+"F0.wireOp",EDGE,"E462"),sQuery(id+"F0.wireOp",EDGE,"E463"),sQuery(id+"F0.wireOp",EDGE,"E464"),sQuery(id+"F0.wireOp",EDGE,"E465"),sQuery(id+"F0.wireOp",EDGE,"E466"),sQuery(id+"F0.wireOp",EDGE,"E467"),sQuery(id+"F0.wireOp",EDGE,"E468"),sQuery(id+"F0.wireOp",EDGE,"E469"),sQuery(id+"F0.wireOp",EDGE,"E470"),sQuery(id+"F0.wireOp",EDGE,"E471"),sQuery(id+"F0.wireOp",EDGE,"E472"),sQuery(id+"F0.wireOp",EDGE,"E473"),sQuery(id+"F0.wireOp",EDGE,"E474"),sQuery(id+"F0.wireOp",EDGE,"E475"),sQuery(id+"F0.wireOp",EDGE,"E476"),sQuery(id+"F0.wireOp",EDGE,"E477"),sQuery(id+"F0.wireOp",EDGE,"E478"),sQuery(id+"F0.wireOp",EDGE,"E479"),sQuery(id+"F0.wireOp",EDGE,"E480"),sQuery(id+"F0.wireOp",EDGE,"E481"),sQuery(id+"F0.wireOp",EDGE,"E482"),sQuery(id+"F0.wireOp",EDGE,"E483"),sQuery(id+"F0.wireOp",EDGE,"E484"),sQuery(id+"F0.wireOp",EDGE,"E485"),sQuery(id+"F0.wireOp",EDGE,"E486"),sQuery(id+"F0.wireOp",EDGE,"E487"),sQuery(id+"F0.wireOp",EDGE,"E488"),sQuery(id+"F0.wireOp",EDGE,"E489"),sQuery(id+"F0.wireOp",EDGE,"E490"),sQuery(id+"F0.wireOp",EDGE,"E491"),sQuery(id+"F0.wireOp",EDGE,"E492"),sQuery(id+"F0.wireOp",EDGE,"E493"),sQuery(id+"F0.wireOp",EDGE,"E494"),sQuery(id+"F0.wireOp",EDGE,"E495.left"),sQuery(id+"F0.wireOp",EDGE,"E495.right"),sQuery(id+"F0.wireOp",EDGE,"E496.bottom"),sQuery(id+"F0.wireOp",EDGE,"E496.top"),sQuery(id+"F0.wireOp",EDGE,"E496.left"),sQuery(id+"F0.wireOp",EDGE,"E496.right"),sQuery(id+"F0.wireOp",EDGE,"E497"),sQuery(id+"F0.wireOp",EDGE,"E498"),sQuery(id+"F0.wireOp",EDGE,"E499"),sQuery(id+"F0.wireOp",EDGE,"E500"),sQuery(id+"F0.wireOp",EDGE,"E501"),sQuery(id+"F0.wireOp",EDGE,"E502"),sQuery(id+"F0.wireOp",EDGE,"E503"),sQuery(id+"F0.wireOp",EDGE,"E504"),sQuery(id+"F0.wireOp",EDGE,"E505"),sQuery(id+"F0.wireOp",EDGE,"E506.bottom"),sQuery(id+"F0.wireOp",EDGE,"E495.top"),sQuery(id+"F0.wireOp",EDGE,"E507.left"),sQuery(id+"F0.wireOp",EDGE,"E507.right")])]});
            var Q1;
            Q1=makeQuery(id+"F1.opExtrude","CAP_EDGE",EDGE,{"disambiguationData":[OSD([sQuery(id+"F0.wireOp",EDGE,"E1.left")])],"isStart":false});
            transform(context, id + "F3", {"entities" : qUnion([Q0]), "transformType" : TransformType.ROTATION, "transformAxis" : qUnion([Q1]), "angle" : 180 * degree, "makeCopy" : false});
        }
        {
            var Q0;
            Q0=makeQuery(id+"F1.opExtrude","CAP_EDGE",EDGE,{"disambiguationData":[OSD([sQuery(id+"F0.wireOp",EDGE,"E1.left")])],"isStart":false});
            cPoint(context, id + "F4", {"entities" : qUnion([Q0]), "parameter" : 0.5});
        }
        {
            var Q0;
            Q0=sQuery(id+"F0.wireOp",EDGE,"E1.right");
            cPoint(context, id + "F5", {"entities" : qUnion([Q0]), "parameter" : 0.5});
        }
        {
            var Q0;
            Q0=makeQuery(id+"F1.opExtrude","SWEPT_BODY",BODY,{"disambiguationData":[OSD([sQuery(id+"F0.wireOp",EDGE,"E0.bottom"),sQuery(id+"F0.wireOp",EDGE,"E0.top"),sQuery(id+"F0.wireOp",EDGE,"E1.left"),sQuery(id+"F0.wireOp",EDGE,"E1.right"),sQuery(id+"F0.wireOp",EDGE,"E2"),sQuery(id+"F0.wireOp",EDGE,"E3"),sQuery(id+"F0.wireOp",EDGE,"E4"),sQuery(id+"F0.wireOp",EDGE,"E5"),sQuery(id+"F0.wireOp",EDGE,"E6"),sQuery(id+"F0.wireOp",EDGE,"E7"),sQuery(id+"F0.wireOp",EDGE,"E8"),sQuery(id+"F0.wireOp",EDGE,"E9"),sQuery(id+"F0.wireOp",EDGE,"E10"),sQuery(id+"F0.wireOp",EDGE,"E11"),sQuery(id+"F0.wireOp",EDGE,"E12"),sQuery(id+"F0.wireOp",EDGE,"E13"),sQuery(id+"F0.wireOp",EDGE,"E14"),sQuery(id+"F0.wireOp",EDGE,"E15"),sQuery(id+"F0.wireOp",EDGE,"E16"),sQuery(id+"F0.wireOp",EDGE,"E17"),sQuery(id+"F0.wireOp",EDGE,"E18"),sQuery(id+"F0.wireOp",EDGE,"E19"),sQuery(id+"F0.wireOp",EDGE,"E20"),sQuery(id+"F0.wireOp",EDGE,"E21"),sQuery(id+"F0.wireOp",EDGE,"E22"),sQuery(id+"F0.wireOp",EDGE,"E23"),sQuery(id+"F0.wireOp",EDGE,"E24"),sQuery(id+"F0.wireOp",EDGE,"E25"),sQuery(id+"F0.wireOp",EDGE,"E26"),sQuery(id+"F0.wireOp",EDGE,"E27"),sQuery(id+"F0.wireOp",EDGE,"E28"),sQuery(id+"F0.wireOp",EDGE,"E29"),sQuery(id+"F0.wireOp",EDGE,"E30"),sQuery(id+"F0.wireOp",EDGE,"E31"),sQuery(id+"F0.wireOp",EDGE,"E32"),sQuery(id+"F0.wireOp",EDGE,"E33"),sQuery(id+"F0.wireOp",EDGE,"E34"),sQuery(id+"F0.wireOp",EDGE,"E35"),sQuery(id+"F0.wireOp",EDGE,"E36"),sQuery(id+"F0.wireOp",EDGE,"E37"),sQuery(id+"F0.wireOp",EDGE,"E38"),sQuery(id+"F0.wireOp",EDGE,"E39"),sQuery(id+"F0.wireOp",EDGE,"E40"),sQuery(id+"F0.wireOp",EDGE,"E41"),sQuery(id+"F0.wireOp",EDGE,"E42"),sQuery(id+"F0.wireOp",EDGE,"E43"),sQuery(id+"F0.wireOp",EDGE,"E44"),sQuery(id+"F0.wireOp",EDGE,"E45"),sQuery(id+"F0.wireOp",EDGE,"E46"),sQuery(id+"F0.wireOp",EDGE,"E47"),sQuery(id+"F0.wireOp",EDGE,"E48"),sQuery(id+"F0.wireOp",EDGE,"E49"),sQuery(id+"F0.wireOp",EDGE,"E50"),sQuery(id+"F0.wireOp",EDGE,"E51"),sQuery(id+"F0.wireOp",EDGE,"E52"),sQuery(id+"F0.wireOp",EDGE,"E53"),sQuery(id+"F0.wireOp",EDGE,"E54"),sQuery(id+"F0.wireOp",EDGE,"E55"),sQuery(id+"F0.wireOp",EDGE,"E56"),sQuery(id+"F0.wireOp",EDGE,"E57"),sQuery(id+"F0.wireOp",EDGE,"E58"),sQuery(id+"F0.wireOp",EDGE,"E59"),sQuery(id+"F0.wireOp",EDGE,"E60"),sQuery(id+"F0.wireOp",EDGE,"E61"),sQuery(id+"F0.wireOp",EDGE,"E62"),sQuery(id+"F0.wireOp",EDGE,"E63"),sQuery(id+"F0.wireOp",EDGE,"E64"),sQuery(id+"F0.wireOp",EDGE,"E65"),sQuery(id+"F0.wireOp",EDGE,"E66"),sQuery(id+"F0.wireOp",EDGE,"E67"),sQuery(id+"F0.wireOp",EDGE,"E68"),sQuery(id+"F0.wireOp",EDGE,"E69"),sQuery(id+"F0.wireOp",EDGE,"E70"),sQuery(id+"F0.wireOp",EDGE,"E71"),sQuery(id+"F0.wireOp",EDGE,"E72"),sQuery(id+"F0.wireOp",EDGE,"E73"),sQuery(id+"F0.wireOp",EDGE,"E74"),sQuery(id+"F0.wireOp",EDGE,"E75"),sQuery(id+"F0.wireOp",EDGE,"E76"),sQuery(id+"F0.wireOp",EDGE,"E77"),sQuery(id+"F0.wireOp",EDGE,"E78"),sQuery(id+"F0.wireOp",EDGE,"E79"),sQuery(id+"F0.wireOp",EDGE,"E80"),sQuery(id+"F0.wireOp",EDGE,"E81"),sQuery(id+"F0.wireOp",EDGE,"E82"),sQuery(id+"F0.wireOp",EDGE,"E83"),sQuery(id+"F0.wireOp",EDGE,"E84"),sQuery(id+"F0.wireOp",EDGE,"E85"),sQuery(id+"F0.wireOp",EDGE,"E86"),sQuery(id+"F0.wireOp",EDGE,"E87"),sQuery(id+"F0.wireOp",EDGE,"E88"),sQuery(id+"F0.wireOp",EDGE,"E89"),sQuery(id+"F0.wireOp",EDGE,"E90"),sQuery(id+"F0.wireOp",EDGE,"E91"),sQuery(id+"F0.wireOp",EDGE,"E92"),sQuery(id+"F0.wireOp",EDGE,"E93"),sQuery(id+"F0.wireOp",EDGE,"E94"),sQuery(id+"F0.wireOp",EDGE,"E95"),sQuery(id+"F0.wireOp",EDGE,"E96"),sQuery(id+"F0.wireOp",EDGE,"E97"),sQuery(id+"F0.wireOp",EDGE,"E98"),sQuery(id+"F0.wireOp",EDGE,"E99"),sQuery(id+"F0.wireOp",EDGE,"E100"),sQuery(id+"F0.wireOp",EDGE,"E101"),sQuery(id+"F0.wireOp",EDGE,"E102"),sQuery(id+"F0.wireOp",EDGE,"E103"),sQuery(id+"F0.wireOp",EDGE,"E104"),sQuery(id+"F0.wireOp",EDGE,"E105"),sQuery(id+"F0.wireOp",EDGE,"E106"),sQuery(id+"F0.wireOp",EDGE,"E107"),sQuery(id+"F0.wireOp",EDGE,"E108"),sQuery(id+"F0.wireOp",EDGE,"E109"),sQuery(id+"F0.wireOp",EDGE,"E110"),sQuery(id+"F0.wireOp",EDGE,"E111"),sQuery(id+"F0.wireOp",EDGE,"E112"),sQuery(id+"F0.wireOp",EDGE,"E113"),sQuery(id+"F0.wireOp",EDGE,"E114"),sQuery(id+"F0.wireOp",EDGE,"E115"),sQuery(id+"F0.wireOp",EDGE,"E116"),sQuery(id+"F0.wireOp",EDGE,"E117"),sQuery(id+"F0.wireOp",EDGE,"E118"),sQuery(id+"F0.wireOp",EDGE,"E119"),sQuery(id+"F0.wireOp",EDGE,"E120"),sQuery(id+"F0.wireOp",EDGE,"E121"),sQuery(id+"F0.wireOp",EDGE,"E122"),sQuery(id+"F0.wireOp",EDGE,"E123"),sQuery(id+"F0.wireOp",EDGE,"E124"),sQuery(id+"F0.wireOp",EDGE,"E125"),sQuery(id+"F0.wireOp",EDGE,"E126"),sQuery(id+"F0.wireOp",EDGE,"E127"),sQuery(id+"F0.wireOp",EDGE,"E128"),sQuery(id+"F0.wireOp",EDGE,"E129"),sQuery(id+"F0.wireOp",EDGE,"E130"),sQuery(id+"F0.wireOp",EDGE,"E131"),sQuery(id+"F0.wireOp",EDGE,"E132"),sQuery(id+"F0.wireOp",EDGE,"E133"),sQuery(id+"F0.wireOp",EDGE,"E134"),sQuery(id+"F0.wireOp",EDGE,"E135"),sQuery(id+"F0.wireOp",EDGE,"E136"),sQuery(id+"F0.wireOp",EDGE,"E137"),sQuery(id+"F0.wireOp",EDGE,"E138"),sQuery(id+"F0.wireOp",EDGE,"E139"),sQuery(id+"F0.wireOp",EDGE,"E140"),sQuery(id+"F0.wireOp",EDGE,"E141"),sQuery(id+"F0.wireOp",EDGE,"E142"),sQuery(id+"F0.wireOp",EDGE,"E143"),sQuery(id+"F0.wireOp",EDGE,"E144"),sQuery(id+"F0.wireOp",EDGE,"E145"),sQuery(id+"F0.wireOp",EDGE,"E146"),sQuery(id+"F0.wireOp",EDGE,"E147"),sQuery(id+"F0.wireOp",EDGE,"E148"),sQuery(id+"F0.wireOp",EDGE,"E149"),sQuery(id+"F0.wireOp",EDGE,"E150"),sQuery(id+"F0.wireOp",EDGE,"E151"),sQuery(id+"F0.wireOp",EDGE,"E152"),sQuery(id+"F0.wireOp",EDGE,"E153"),sQuery(id+"F0.wireOp",EDGE,"E154"),sQuery(id+"F0.wireOp",EDGE,"E155"),sQuery(id+"F0.wireOp",EDGE,"E156"),sQuery(id+"F0.wireOp",EDGE,"E157"),sQuery(id+"F0.wireOp",EDGE,"E158"),sQuery(id+"F0.wireOp",EDGE,"E159"),sQuery(id+"F0.wireOp",EDGE,"E160"),sQuery(id+"F0.wireOp",EDGE,"E161"),sQuery(id+"F0.wireOp",EDGE,"E162"),sQuery(id+"F0.wireOp",EDGE,"E163"),sQuery(id+"F0.wireOp",EDGE,"E164"),sQuery(id+"F0.wireOp",EDGE,"E165"),sQuery(id+"F0.wireOp",EDGE,"E166"),sQuery(id+"F0.wireOp",EDGE,"E167"),sQuery(id+"F0.wireOp",EDGE,"E168"),sQuery(id+"F0.wireOp",EDGE,"E169"),sQuery(id+"F0.wireOp",EDGE,"E170"),sQuery(id+"F0.wireOp",EDGE,"E171"),sQuery(id+"F0.wireOp",EDGE,"E172"),sQuery(id+"F0.wireOp",EDGE,"E173"),sQuery(id+"F0.wireOp",EDGE,"E174"),sQuery(id+"F0.wireOp",EDGE,"E175"),sQuery(id+"F0.wireOp",EDGE,"E176"),sQuery(id+"F0.wireOp",EDGE,"E177"),sQuery(id+"F0.wireOp",EDGE,"E178"),sQuery(id+"F0.wireOp",EDGE,"E179"),sQuery(id+"F0.wireOp",EDGE,"E180"),sQuery(id+"F0.wireOp",EDGE,"E181"),sQuery(id+"F0.wireOp",EDGE,"E182"),sQuery(id+"F0.wireOp",EDGE,"E183"),sQuery(id+"F0.wireOp",EDGE,"E184"),sQuery(id+"F0.wireOp",EDGE,"E185"),sQuery(id+"F0.wireOp",EDGE,"E186"),sQuery(id+"F0.wireOp",EDGE,"E187"),sQuery(id+"F0.wireOp",EDGE,"E188"),sQuery(id+"F0.wireOp",EDGE,"E189"),sQuery(id+"F0.wireOp",EDGE,"E190"),sQuery(id+"F0.wireOp",EDGE,"E191"),sQuery(id+"F0.wireOp",EDGE,"E192"),sQuery(id+"F0.wireOp",EDGE,"E193"),sQuery(id+"F0.wireOp",EDGE,"E194"),sQuery(id+"F0.wireOp",EDGE,"E195"),sQuery(id+"F0.wireOp",EDGE,"E196"),sQuery(id+"F0.wireOp",EDGE,"E197"),sQuery(id+"F0.wireOp",EDGE,"E198"),sQuery(id+"F0.wireOp",EDGE,"E199"),sQuery(id+"F0.wireOp",EDGE,"E200"),sQuery(id+"F0.wireOp",EDGE,"E201"),sQuery(id+"F0.wireOp",EDGE,"E202"),sQuery(id+"F0.wireOp",EDGE,"E203"),sQuery(id+"F0.wireOp",EDGE,"E204"),sQuery(id+"F0.wireOp",EDGE,"E205"),sQuery(id+"F0.wireOp",EDGE,"E206"),sQuery(id+"F0.wireOp",EDGE,"E207"),sQuery(id+"F0.wireOp",EDGE,"E208"),sQuery(id+"F0.wireOp",EDGE,"E209"),sQuery(id+"F0.wireOp",EDGE,"E210"),sQuery(id+"F0.wireOp",EDGE,"E211"),sQuery(id+"F0.wireOp",EDGE,"E212"),sQuery(id+"F0.wireOp",EDGE,"E213"),sQuery(id+"F0.wireOp",EDGE,"E214"),sQuery(id+"F0.wireOp",EDGE,"E215"),sQuery(id+"F0.wireOp",EDGE,"E216"),sQuery(id+"F0.wireOp",EDGE,"E217"),sQuery(id+"F0.wireOp",EDGE,"E218"),sQuery(id+"F0.wireOp",EDGE,"E219"),sQuery(id+"F0.wireOp",EDGE,"E220"),sQuery(id+"F0.wireOp",EDGE,"E221"),sQuery(id+"F0.wireOp",EDGE,"E222"),sQuery(id+"F0.wireOp",EDGE,"E223"),sQuery(id+"F0.wireOp",EDGE,"E224"),sQuery(id+"F0.wireOp",EDGE,"E225"),sQuery(id+"F0.wireOp",EDGE,"E226"),sQuery(id+"F0.wireOp",EDGE,"E227"),sQuery(id+"F0.wireOp",EDGE,"E228"),sQuery(id+"F0.wireOp",EDGE,"E229"),sQuery(id+"F0.wireOp",EDGE,"E230"),sQuery(id+"F0.wireOp",EDGE,"E231"),sQuery(id+"F0.wireOp",EDGE,"E232"),sQuery(id+"F0.wireOp",EDGE,"E233"),sQuery(id+"F0.wireOp",EDGE,"E234"),sQuery(id+"F0.wireOp",EDGE,"E235"),sQuery(id+"F0.wireOp",EDGE,"E236"),sQuery(id+"F0.wireOp",EDGE,"E237"),sQuery(id+"F0.wireOp",EDGE,"E238"),sQuery(id+"F0.wireOp",EDGE,"E239"),sQuery(id+"F0.wireOp",EDGE,"E240"),sQuery(id+"F0.wireOp",EDGE,"E241"),sQuery(id+"F0.wireOp",EDGE,"E242"),sQuery(id+"F0.wireOp",EDGE,"E243"),sQuery(id+"F0.wireOp",EDGE,"E244"),sQuery(id+"F0.wireOp",EDGE,"E245"),sQuery(id+"F0.wireOp",EDGE,"E246"),sQuery(id+"F0.wireOp",EDGE,"E247"),sQuery(id+"F0.wireOp",EDGE,"E248"),sQuery(id+"F0.wireOp",EDGE,"E249"),sQuery(id+"F0.wireOp",EDGE,"E250"),sQuery(id+"F0.wireOp",EDGE,"E251"),sQuery(id+"F0.wireOp",EDGE,"E252"),sQuery(id+"F0.wireOp",EDGE,"E253"),sQuery(id+"F0.wireOp",EDGE,"E254"),sQuery(id+"F0.wireOp",EDGE,"E255"),sQuery(id+"F0.wireOp",EDGE,"E256"),sQuery(id+"F0.wireOp",EDGE,"E257"),sQuery(id+"F0.wireOp",EDGE,"E258"),sQuery(id+"F0.wireOp",EDGE,"E259"),sQuery(id+"F0.wireOp",EDGE,"E260"),sQuery(id+"F0.wireOp",EDGE,"E261"),sQuery(id+"F0.wireOp",EDGE,"E262"),sQuery(id+"F0.wireOp",EDGE,"E263"),sQuery(id+"F0.wireOp",EDGE,"E264"),sQuery(id+"F0.wireOp",EDGE,"E265"),sQuery(id+"F0.wireOp",EDGE,"E266"),sQuery(id+"F0.wireOp",EDGE,"E267"),sQuery(id+"F0.wireOp",EDGE,"E268"),sQuery(id+"F0.wireOp",EDGE,"E269"),sQuery(id+"F0.wireOp",EDGE,"E270"),sQuery(id+"F0.wireOp",EDGE,"E271"),sQuery(id+"F0.wireOp",EDGE,"E272"),sQuery(id+"F0.wireOp",EDGE,"E273"),sQuery(id+"F0.wireOp",EDGE,"E274"),sQuery(id+"F0.wireOp",EDGE,"E275"),sQuery(id+"F0.wireOp",EDGE,"E276"),sQuery(id+"F0.wireOp",EDGE,"E277"),sQuery(id+"F0.wireOp",EDGE,"E278"),sQuery(id+"F0.wireOp",EDGE,"E279"),sQuery(id+"F0.wireOp",EDGE,"E280"),sQuery(id+"F0.wireOp",EDGE,"E281"),sQuery(id+"F0.wireOp",EDGE,"E282"),sQuery(id+"F0.wireOp",EDGE,"E283"),sQuery(id+"F0.wireOp",EDGE,"E284"),sQuery(id+"F0.wireOp",EDGE,"E285"),sQuery(id+"F0.wireOp",EDGE,"E286"),sQuery(id+"F0.wireOp",EDGE,"E287"),sQuery(id+"F0.wireOp",EDGE,"E288"),sQuery(id+"F0.wireOp",EDGE,"E289"),sQuery(id+"F0.wireOp",EDGE,"E290"),sQuery(id+"F0.wireOp",EDGE,"E291"),sQuery(id+"F0.wireOp",EDGE,"E292"),sQuery(id+"F0.wireOp",EDGE,"E293"),sQuery(id+"F0.wireOp",EDGE,"E294"),sQuery(id+"F0.wireOp",EDGE,"E295"),sQuery(id+"F0.wireOp",EDGE,"E296"),sQuery(id+"F0.wireOp",EDGE,"E297"),sQuery(id+"F0.wireOp",EDGE,"E298"),sQuery(id+"F0.wireOp",EDGE,"E299"),sQuery(id+"F0.wireOp",EDGE,"E300"),sQuery(id+"F0.wireOp",EDGE,"E301"),sQuery(id+"F0.wireOp",EDGE,"E302"),sQuery(id+"F0.wireOp",EDGE,"E303"),sQuery(id+"F0.wireOp",EDGE,"E304"),sQuery(id+"F0.wireOp",EDGE,"E305"),sQuery(id+"F0.wireOp",EDGE,"E306"),sQuery(id+"F0.wireOp",EDGE,"E307"),sQuery(id+"F0.wireOp",EDGE,"E308"),sQuery(id+"F0.wireOp",EDGE,"E309"),sQuery(id+"F0.wireOp",EDGE,"E310"),sQuery(id+"F0.wireOp",EDGE,"E311"),sQuery(id+"F0.wireOp",EDGE,"E312"),sQuery(id+"F0.wireOp",EDGE,"E313"),sQuery(id+"F0.wireOp",EDGE,"E314"),sQuery(id+"F0.wireOp",EDGE,"E315"),sQuery(id+"F0.wireOp",EDGE,"E316"),sQuery(id+"F0.wireOp",EDGE,"E317"),sQuery(id+"F0.wireOp",EDGE,"E318"),sQuery(id+"F0.wireOp",EDGE,"E319"),sQuery(id+"F0.wireOp",EDGE,"E320"),sQuery(id+"F0.wireOp",EDGE,"E321"),sQuery(id+"F0.wireOp",EDGE,"E322"),sQuery(id+"F0.wireOp",EDGE,"E323"),sQuery(id+"F0.wireOp",EDGE,"E324"),sQuery(id+"F0.wireOp",EDGE,"E325"),sQuery(id+"F0.wireOp",EDGE,"E326"),sQuery(id+"F0.wireOp",EDGE,"E327"),sQuery(id+"F0.wireOp",EDGE,"E328"),sQuery(id+"F0.wireOp",EDGE,"E329"),sQuery(id+"F0.wireOp",EDGE,"E330"),sQuery(id+"F0.wireOp",EDGE,"E331"),sQuery(id+"F0.wireOp",EDGE,"E332"),sQuery(id+"F0.wireOp",EDGE,"E333"),sQuery(id+"F0.wireOp",EDGE,"E334"),sQuery(id+"F0.wireOp",EDGE,"E335"),sQuery(id+"F0.wireOp",EDGE,"E336"),sQuery(id+"F0.wireOp",EDGE,"E337"),sQuery(id+"F0.wireOp",EDGE,"E338"),sQuery(id+"F0.wireOp",EDGE,"E339"),sQuery(id+"F0.wireOp",EDGE,"E340"),sQuery(id+"F0.wireOp",EDGE,"E341"),sQuery(id+"F0.wireOp",EDGE,"E342"),sQuery(id+"F0.wireOp",EDGE,"E343"),sQuery(id+"F0.wireOp",EDGE,"E344"),sQuery(id+"F0.wireOp",EDGE,"E345"),sQuery(id+"F0.wireOp",EDGE,"E346"),sQuery(id+"F0.wireOp",EDGE,"E347"),sQuery(id+"F0.wireOp",EDGE,"E348"),sQuery(id+"F0.wireOp",EDGE,"E349"),sQuery(id+"F0.wireOp",EDGE,"E350"),sQuery(id+"F0.wireOp",EDGE,"E351"),sQuery(id+"F0.wireOp",EDGE,"E352"),sQuery(id+"F0.wireOp",EDGE,"E353"),sQuery(id+"F0.wireOp",EDGE,"E354"),sQuery(id+"F0.wireOp",EDGE,"E355"),sQuery(id+"F0.wireOp",EDGE,"E356"),sQuery(id+"F0.wireOp",EDGE,"E357"),sQuery(id+"F0.wireOp",EDGE,"E358"),sQuery(id+"F0.wireOp",EDGE,"E359"),sQuery(id+"F0.wireOp",EDGE,"E360"),sQuery(id+"F0.wireOp",EDGE,"E361"),sQuery(id+"F0.wireOp",EDGE,"E362"),sQuery(id+"F0.wireOp",EDGE,"E363"),sQuery(id+"F0.wireOp",EDGE,"E364"),sQuery(id+"F0.wireOp",EDGE,"E365"),sQuery(id+"F0.wireOp",EDGE,"E366"),sQuery(id+"F0.wireOp",EDGE,"E367"),sQuery(id+"F0.wireOp",EDGE,"E368"),sQuery(id+"F0.wireOp",EDGE,"E369"),sQuery(id+"F0.wireOp",EDGE,"E370"),sQuery(id+"F0.wireOp",EDGE,"E371"),sQuery(id+"F0.wireOp",EDGE,"E372"),sQuery(id+"F0.wireOp",EDGE,"E373"),sQuery(id+"F0.wireOp",EDGE,"E374"),sQuery(id+"F0.wireOp",EDGE,"E375"),sQuery(id+"F0.wireOp",EDGE,"E376"),sQuery(id+"F0.wireOp",EDGE,"E377"),sQuery(id+"F0.wireOp",EDGE,"E378"),sQuery(id+"F0.wireOp",EDGE,"E379"),sQuery(id+"F0.wireOp",EDGE,"E380"),sQuery(id+"F0.wireOp",EDGE,"E381"),sQuery(id+"F0.wireOp",EDGE,"E382"),sQuery(id+"F0.wireOp",EDGE,"E383"),sQuery(id+"F0.wireOp",EDGE,"E384"),sQuery(id+"F0.wireOp",EDGE,"E385"),sQuery(id+"F0.wireOp",EDGE,"E386"),sQuery(id+"F0.wireOp",EDGE,"E387"),sQuery(id+"F0.wireOp",EDGE,"E388"),sQuery(id+"F0.wireOp",EDGE,"E389"),sQuery(id+"F0.wireOp",EDGE,"E390"),sQuery(id+"F0.wireOp",EDGE,"E391"),sQuery(id+"F0.wireOp",EDGE,"E392"),sQuery(id+"F0.wireOp",EDGE,"E393"),sQuery(id+"F0.wireOp",EDGE,"E394"),sQuery(id+"F0.wireOp",EDGE,"E395"),sQuery(id+"F0.wireOp",EDGE,"E396"),sQuery(id+"F0.wireOp",EDGE,"E397"),sQuery(id+"F0.wireOp",EDGE,"E398"),sQuery(id+"F0.wireOp",EDGE,"E399"),sQuery(id+"F0.wireOp",EDGE,"E400"),sQuery(id+"F0.wireOp",EDGE,"E401"),sQuery(id+"F0.wireOp",EDGE,"E402"),sQuery(id+"F0.wireOp",EDGE,"E403"),sQuery(id+"F0.wireOp",EDGE,"E404"),sQuery(id+"F0.wireOp",EDGE,"E405"),sQuery(id+"F0.wireOp",EDGE,"E406"),sQuery(id+"F0.wireOp",EDGE,"E407"),sQuery(id+"F0.wireOp",EDGE,"E408"),sQuery(id+"F0.wireOp",EDGE,"E409"),sQuery(id+"F0.wireOp",EDGE,"E410"),sQuery(id+"F0.wireOp",EDGE,"E411"),sQuery(id+"F0.wireOp",EDGE,"E412"),sQuery(id+"F0.wireOp",EDGE,"E413"),sQuery(id+"F0.wireOp",EDGE,"E414"),sQuery(id+"F0.wireOp",EDGE,"E415"),sQuery(id+"F0.wireOp",EDGE,"E416"),sQuery(id+"F0.wireOp",EDGE,"E417"),sQuery(id+"F0.wireOp",EDGE,"E418"),sQuery(id+"F0.wireOp",EDGE,"E419"),sQuery(id+"F0.wireOp",EDGE,"E420"),sQuery(id+"F0.wireOp",EDGE,"E421"),sQuery(id+"F0.wireOp",EDGE,"E422"),sQuery(id+"F0.wireOp",EDGE,"E423"),sQuery(id+"F0.wireOp",EDGE,"E424"),sQuery(id+"F0.wireOp",EDGE,"E425"),sQuery(id+"F0.wireOp",EDGE,"E426"),sQuery(id+"F0.wireOp",EDGE,"E427"),sQuery(id+"F0.wireOp",EDGE,"E428"),sQuery(id+"F0.wireOp",EDGE,"E429"),sQuery(id+"F0.wireOp",EDGE,"E430"),sQuery(id+"F0.wireOp",EDGE,"E431"),sQuery(id+"F0.wireOp",EDGE,"E432"),sQuery(id+"F0.wireOp",EDGE,"E433"),sQuery(id+"F0.wireOp",EDGE,"E434"),sQuery(id+"F0.wireOp",EDGE,"E435"),sQuery(id+"F0.wireOp",EDGE,"E436"),sQuery(id+"F0.wireOp",EDGE,"E437"),sQuery(id+"F0.wireOp",EDGE,"E438"),sQuery(id+"F0.wireOp",EDGE,"E439"),sQuery(id+"F0.wireOp",EDGE,"E440"),sQuery(id+"F0.wireOp",EDGE,"E441"),sQuery(id+"F0.wireOp",EDGE,"E442"),sQuery(id+"F0.wireOp",EDGE,"E443"),sQuery(id+"F0.wireOp",EDGE,"E444"),sQuery(id+"F0.wireOp",EDGE,"E445"),sQuery(id+"F0.wireOp",EDGE,"E446"),sQuery(id+"F0.wireOp",EDGE,"E447"),sQuery(id+"F0.wireOp",EDGE,"E448"),sQuery(id+"F0.wireOp",EDGE,"E449"),sQuery(id+"F0.wireOp",EDGE,"E450"),sQuery(id+"F0.wireOp",EDGE,"E451"),sQuery(id+"F0.wireOp",EDGE,"E452"),sQuery(id+"F0.wireOp",EDGE,"E453"),sQuery(id+"F0.wireOp",EDGE,"E454"),sQuery(id+"F0.wireOp",EDGE,"E455"),sQuery(id+"F0.wireOp",EDGE,"E456"),sQuery(id+"F0.wireOp",EDGE,"E457"),sQuery(id+"F0.wireOp",EDGE,"E458"),sQuery(id+"F0.wireOp",EDGE,"E459"),sQuery(id+"F0.wireOp",EDGE,"E460"),sQuery(id+"F0.wireOp",EDGE,"E461"),sQuery(id+"F0.wireOp",EDGE,"E462"),sQuery(id+"F0.wireOp",EDGE,"E463"),sQuery(id+"F0.wireOp",EDGE,"E464"),sQuery(id+"F0.wireOp",EDGE,"E465"),sQuery(id+"F0.wireOp",EDGE,"E466"),sQuery(id+"F0.wireOp",EDGE,"E467"),sQuery(id+"F0.wireOp",EDGE,"E468"),sQuery(id+"F0.wireOp",EDGE,"E469"),sQuery(id+"F0.wireOp",EDGE,"E470"),sQuery(id+"F0.wireOp",EDGE,"E471"),sQuery(id+"F0.wireOp",EDGE,"E472"),sQuery(id+"F0.wireOp",EDGE,"E473"),sQuery(id+"F0.wireOp",EDGE,"E474"),sQuery(id+"F0.wireOp",EDGE,"E475"),sQuery(id+"F0.wireOp",EDGE,"E476"),sQuery(id+"F0.wireOp",EDGE,"E477"),sQuery(id+"F0.wireOp",EDGE,"E478"),sQuery(id+"F0.wireOp",EDGE,"E479"),sQuery(id+"F0.wireOp",EDGE,"E480"),sQuery(id+"F0.wireOp",EDGE,"E481"),sQuery(id+"F0.wireOp",EDGE,"E482"),sQuery(id+"F0.wireOp",EDGE,"E483"),sQuery(id+"F0.wireOp",EDGE,"E484"),sQuery(id+"F0.wireOp",EDGE,"E485"),sQuery(id+"F0.wireOp",EDGE,"E486"),sQuery(id+"F0.wireOp",EDGE,"E487"),sQuery(id+"F0.wireOp",EDGE,"E488"),sQuery(id+"F0.wireOp",EDGE,"E489"),sQuery(id+"F0.wireOp",EDGE,"E490"),sQuery(id+"F0.wireOp",EDGE,"E491"),sQuery(id+"F0.wireOp",EDGE,"E492"),sQuery(id+"F0.wireOp",EDGE,"E493"),sQuery(id+"F0.wireOp",EDGE,"E494"),sQuery(id+"F0.wireOp",EDGE,"E495.left"),sQuery(id+"F0.wireOp",EDGE,"E495.right"),sQuery(id+"F0.wireOp",EDGE,"E496.bottom"),sQuery(id+"F0.wireOp",EDGE,"E496.top"),sQuery(id+"F0.wireOp",EDGE,"E496.left"),sQuery(id+"F0.wireOp",EDGE,"E496.right"),sQuery(id+"F0.wireOp",EDGE,"E497"),sQuery(id+"F0.wireOp",EDGE,"E498"),sQuery(id+"F0.wireOp",EDGE,"E499"),sQuery(id+"F0.wireOp",EDGE,"E500"),sQuery(id+"F0.wireOp",EDGE,"E501"),sQuery(id+"F0.wireOp",EDGE,"E502"),sQuery(id+"F0.wireOp",EDGE,"E503"),sQuery(id+"F0.wireOp",EDGE,"E504"),sQuery(id+"F0.wireOp",EDGE,"E505"),sQuery(id+"F0.wireOp",EDGE,"E506.bottom"),sQuery(id+"F0.wireOp",EDGE,"E495.top"),sQuery(id+"F0.wireOp",EDGE,"E507.left"),sQuery(id+"F0.wireOp",EDGE,"E507.right")])]});
            var Q1;
            Q1 = qCreatedBy(id + "F4" ,VERTEX);
            var Q2;
            Q2 = qCreatedBy(id + "F5" ,VERTEX);
            transform(context, id + "F6", {"entities" : qUnion([Q0]), "transformType" : TransformType.TRANSLATION_ENTITY, "oppositeDirectionEntity" : false, "transformLine" : qUnion([Q1, Q2]), "makeCopy" : false});
        }
        {
            var Q0;
            Q0=makeQuery(id+"F1.opExtrude","CAP_EDGE",EDGE,{"disambiguationData":[OSD([sQuery(id+"F0.wireOp",EDGE,"E505")])],"isStart":true});
            var Q1;
            Q1=makeQuery(id+"F1.opExtrude","CAP_EDGE",EDGE,{"disambiguationData":[OSD([sQuery(id+"F0.wireOp",EDGE,"E502")])],"isStart":true});
            var Q2;
            Q2=makeQuery(id+"F1.opExtrude","CAP_EDGE",EDGE,{"disambiguationData":[OSD([sQuery(id+"F0.wireOp",EDGE,"E504")])],"isStart":true});
            var Q3;
            Q3=makeQuery(id+"F1.opExtrude","CAP_EDGE",EDGE,{"disambiguationData":[OSD([sQuery(id+"F0.wireOp",EDGE,"E501")])],"isStart":true});
            var Q4;
            Q4=makeQuery(id+"F1.opExtrude","CAP_EDGE",EDGE,{"disambiguationData":[OSD([sQuery(id+"F0.wireOp",EDGE,"E499")])],"isStart":true});
            var Q5;
            Q5=makeQuery(id+"F1.opExtrude","CAP_EDGE",EDGE,{"disambiguationData":[OSD([sQuery(id+"F0.wireOp",EDGE,"E498")])],"isStart":true});
            var Q6;
            Q6=makeQuery(id+"F1.opExtrude","CAP_EDGE",EDGE,{"disambiguationData":[OSD([sQuery(id+"F0.wireOp",EDGE,"E500")])],"isStart":true});
            var Q7;
            Q7=makeQuery(id+"F1.opExtrude","CAP_EDGE",EDGE,{"disambiguationData":[OSD([sQuery(id+"F0.wireOp",EDGE,"E497")])],"isStart":true});
            chamfer(context, id + "F7", {"entities" : qUnion([Q0, Q1, Q2, Q3, Q4, Q5, Q6, Q7]), "width" : 0.89 * mm, "tangentPropagation" : true});
        }
        {
            var Q0;
            Q0=makeQuery(id+"F1.opExtrude","CAP_EDGE",EDGE,{"disambiguationData":[OSD([sQuery(id+"F0.wireOp",EDGE,"E496.top")])],"isStart":true});
            var Q1;
            Q1=makeQuery(id+"F1.opExtrude","CAP_EDGE",EDGE,{"disambiguationData":[OSD([sQuery(id+"F0.wireOp",EDGE,"E496.left")])],"isStart":true});
            var Q2;
            Q2=makeQuery(id+"F1.opExtrude","CAP_EDGE",EDGE,{"disambiguationData":[OSD([sQuery(id+"F0.wireOp",EDGE,"E496.bottom")])],"isStart":true});
            var Q3;
            Q3=makeQuery(id+"F1.opExtrude","CAP_EDGE",EDGE,{"disambiguationData":[OSD([sQuery(id+"F0.wireOp",EDGE,"E496.right")])],"isStart":true});
            var Q4;
            Q4=makeQuery(id+"F1.opExtrude","CAP_EDGE",EDGE,{"disambiguationData":[OSD([sQuery(id+"F0.wireOp",EDGE,"E495.right"),sQuery(id+"F0.wireOp",EDGE,"E507.right")])],"isStart":true});
            var Q5;
            Q5=makeQuery(id+"F1.opExtrude","CAP_EDGE",EDGE,{"disambiguationData":[OSD([sQuery(id+"F0.wireOp",EDGE,"E506.bottom")])],"isStart":true});
            var Q6;
            Q6=makeQuery(id+"F1.opExtrude","CAP_EDGE",EDGE,{"disambiguationData":[OSD([sQuery(id+"F0.wireOp",EDGE,"E495.left"),sQuery(id+"F0.wireOp",EDGE,"E507.left")])],"isStart":true});
            var Q7;
            Q7=makeQuery(id+"F1.opExtrude","CAP_EDGE",EDGE,{"disambiguationData":[OSD([sQuery(id+"F0.wireOp",EDGE,"E495.top")])],"isStart":true});
            chamfer(context, id + "F8", {"entities" : qUnion([Q0, Q1, Q2, Q3, Q4, Q5, Q6, Q7]), "width" : 0.25 * mm, "tangentPropagation" : true});
        }
        {
            var Q0;
            Q0=makeQuery(id+"F1.opExtrude","CAP_EDGE",EDGE,{"disambiguationData":[OSD([sQuery(id+"F0.wireOp",EDGE,"E1.right")])],"isStart":true});
            var Q1;
            Q1=makeQuery(id+"F1.opExtrude","CAP_EDGE",EDGE,{"disambiguationData":[OSD([sQuery(id+"F0.wireOp",EDGE,"E3")])],"isStart":true});
            var Q2;
            Q2=makeQuery(id+"F1.opExtrude","CAP_EDGE",EDGE,{"disambiguationData":[OSD([sQuery(id+"F0.wireOp",EDGE,"E0.bottom")])],"isStart":true});
            var Q3;
            Q3=makeQuery(id+"F1.opExtrude","CAP_EDGE",EDGE,{"disambiguationData":[OSD([sQuery(id+"F0.wireOp",EDGE,"E2")])],"isStart":true});
            var Q4;
            Q4=makeQuery(id+"F1.opExtrude","CAP_EDGE",EDGE,{"disambiguationData":[OSD([sQuery(id+"F0.wireOp",EDGE,"E1.left")])],"isStart":true});
            var Q5;
            Q5=makeQuery(id+"F1.opExtrude","CAP_EDGE",EDGE,{"disambiguationData":[OSD([sQuery(id+"F0.wireOp",EDGE,"E5")])],"isStart":true});
            var Q6;
            Q6=makeQuery(id+"F1.opExtrude","CAP_EDGE",EDGE,{"disambiguationData":[OSD([sQuery(id+"F0.wireOp",EDGE,"E0.top")])],"isStart":true});
            var Q7;
            Q7=makeQuery(id+"F1.opExtrude","CAP_EDGE",EDGE,{"disambiguationData":[OSD([sQuery(id+"F0.wireOp",EDGE,"E4")])],"isStart":true});
            chamfer(context, id + "F9", {"entities" : qUnion([Q0, Q1, Q2, Q3, Q4, Q5, Q6, Q7]), "chamferType" : ChamferType.TWO_OFFSETS, "width1" : 7.62 * mm, "oppositeDirection" : false, "width2" : 6.35 * mm, "tangentPropagation" : true});
        }
    });
